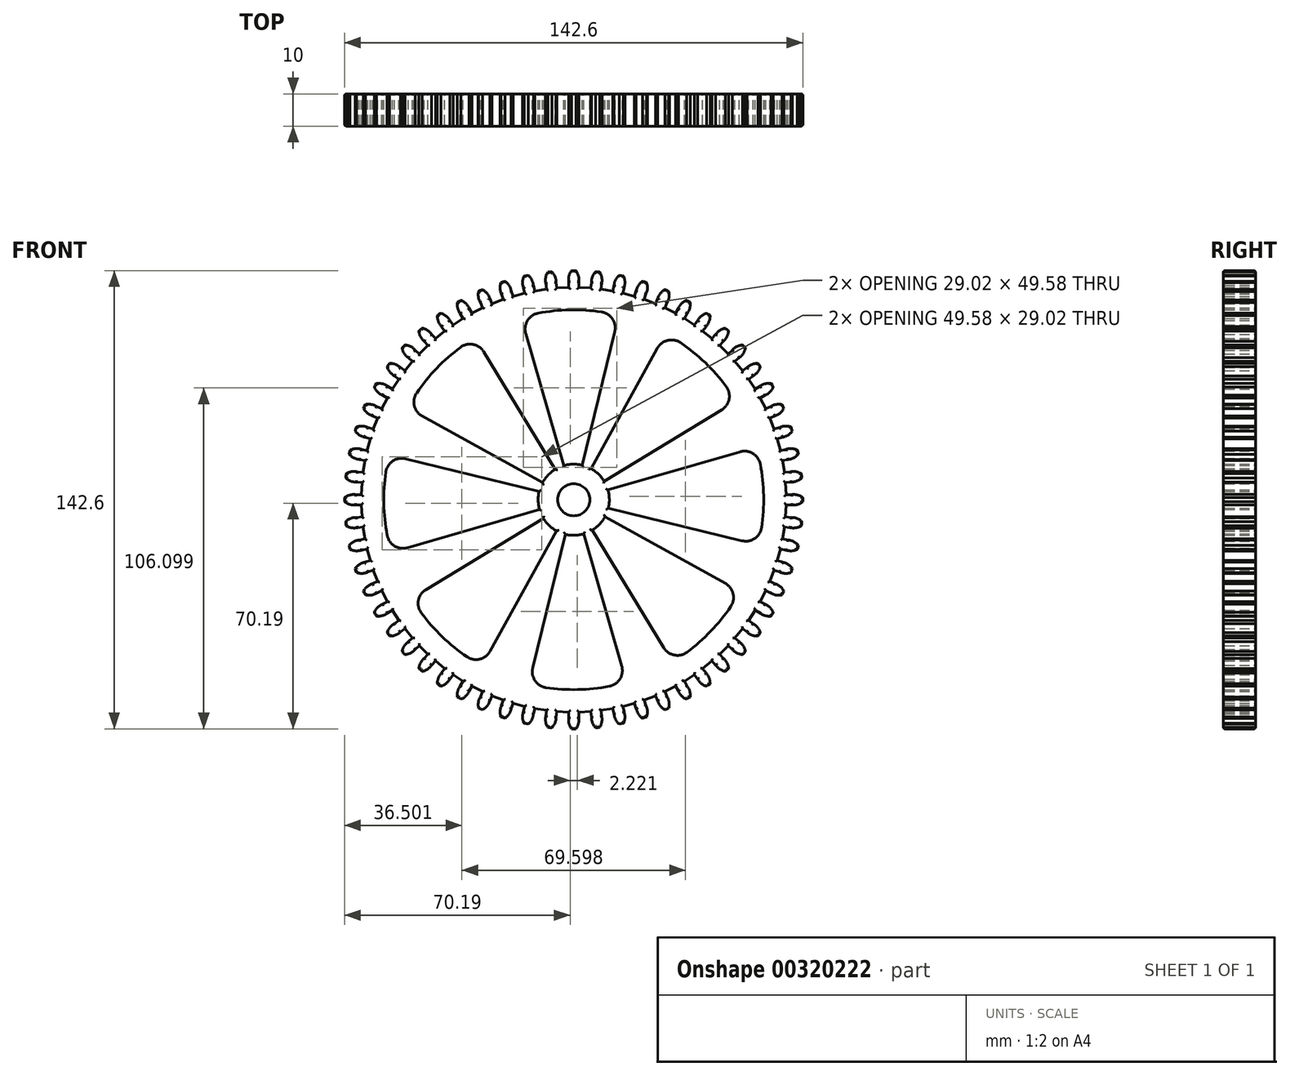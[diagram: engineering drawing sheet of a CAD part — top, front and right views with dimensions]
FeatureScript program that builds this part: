
annotation { "Feature Type Name" : "Feature", "Feature Type Description" : "" }
export const myFeature = defineFeature(function(context is Context, id is Id, definition is map)
    precondition{}
    {
        {
            var Q0;
            Q0=qCreatedBy(makeId("Front.planeOp"),FACE);
            var sketch = newSketch(context, id + "F0", { "sketchPlane" : qUnion([Q0])});
            skCircle(sketch, "E0", {"center": v(0, 0) * mm, "radius": 5 * mm});
            skLineSegment(sketch, "E1", {"start": v(1.6, 66.08) * mm, "end": v(1.6, 68.99) * mm});
            skArc(sketch, "E2", {"start": v(1.6, 67.83) * mm, "mid": v(1.47, 69.66) * mm, "end": v(0.66, 71.3) * mm});
            skLineSegment(sketch, "E3", {"start": v(0, 71.3) * mm, "end": v(0.66, 71.3) * mm});
            skLineSegment(sketch, "E4.MirrorCS", {"start": v(0, 71.3) * mm, "end": v(-0.66, 71.3) * mm});
            skArc(sketch, "E5.MirrorCS", {"start": v(-1.6, 67.83) * mm, "mid": v(-1.47, 69.66) * mm, "end": v(-0.66, 71.3) * mm});
            skLineSegment(sketch, "E6.MirrorCS", {"start": v(-1.6, 66.08) * mm, "end": v(-1.6, 68.99) * mm});
            skLineSegment(sketch, "E7.1.0", {"start": v(-8.5, 65.55) * mm, "end": v(-8.8, 68.44) * mm});
            skArc(sketch, "E7.1.1", {"start": v(-8.68, 67.3) * mm, "mid": v(-8.74, 69.12) * mm, "end": v(-8.1, 70.84) * mm});
            skLineSegment(sketch, "E7.1.2", {"start": v(-7.45, 70.9) * mm, "end": v(-8.1, 70.84) * mm});
            skLineSegment(sketch, "E7.1.3", {"start": v(-7.45, 70.9) * mm, "end": v(-6.8, 70.98) * mm});
            skArc(sketch, "E7.1.4", {"start": v(-5.5, 67.63) * mm, "mid": v(-5.82, 69.43) * mm, "end": v(-6.8, 70.98) * mm});
            skLineSegment(sketch, "E7.1.5", {"start": v(-5.32, 65.89) * mm, "end": v(-5.62, 68.78) * mm});
            skLineSegment(sketch, "E7.2.0", {"start": v(-15.3, 64.3) * mm, "end": v(-15.9, 67.15) * mm});
            skArc(sketch, "E7.2.1", {"start": v(-15.67, 66.02) * mm, "mid": v(-15.92, 67.83) * mm, "end": v(-15.47, 69.6) * mm});
            skLineSegment(sketch, "E7.2.2", {"start": v(-14.82, 69.74) * mm, "end": v(-15.47, 69.6) * mm});
            skLineSegment(sketch, "E7.2.3", {"start": v(-14.82, 69.74) * mm, "end": v(-14.18, 69.88) * mm});
            skArc(sketch, "E7.2.4", {"start": v(-12.54, 66.68) * mm, "mid": v(-13.05, 68.44) * mm, "end": v(-14.18, 69.88) * mm});
            skLineSegment(sketch, "E7.2.5", {"start": v(-12.17, 64.97) * mm, "end": v(-12.78, 67.81) * mm});
            skLineSegment(sketch, "E7.3.0", {"start": v(-21.94, 62.35) * mm, "end": v(-22.84, 65.12) * mm});
            skArc(sketch, "E7.3.1", {"start": v(-22.48, 64.02) * mm, "mid": v(-22.92, 65.8) * mm, "end": v(-22.66, 67.6) * mm});
            skLineSegment(sketch, "E7.3.2", {"start": v(-22.03, 67.81) * mm, "end": v(-22.66, 67.6) * mm});
            skLineSegment(sketch, "E7.3.3", {"start": v(-22.03, 67.81) * mm, "end": v(-21.4, 68.01) * mm});
            skArc(sketch, "E7.3.4", {"start": v(-19.44, 65) * mm, "mid": v(-20.13, 66.7) * mm, "end": v(-21.4, 68.01) * mm});
            skLineSegment(sketch, "E7.3.5", {"start": v(-18.9, 63.34) * mm, "end": v(-19.8, 66.1) * mm});
            skLineSegment(sketch, "E7.4.0", {"start": v(-28.34, 59.72) * mm, "end": v(-29.52, 62.37) * mm});
            skArc(sketch, "E7.4.1", {"start": v(-29.05, 61.32) * mm, "mid": v(-29.67, 63.04) * mm, "end": v(-29.6, 64.87) * mm});
            skLineSegment(sketch, "E7.4.2", {"start": v(-29, 65.14) * mm, "end": v(-29.6, 64.87) * mm});
            skLineSegment(sketch, "E7.4.3", {"start": v(-29, 65.14) * mm, "end": v(-28.4, 65.4) * mm});
            skArc(sketch, "E7.4.4", {"start": v(-26.13, 62.62) * mm, "mid": v(-26.99, 64.23) * mm, "end": v(-28.4, 65.4) * mm});
            skLineSegment(sketch, "E7.4.5", {"start": v(-25.42, 61.02) * mm, "end": v(-26.6, 63.68) * mm});
            skLineSegment(sketch, "E7.5.0", {"start": v(-34.43, 56.43) * mm, "end": v(-35.88, 58.95) * mm});
            skArc(sketch, "E7.5.1", {"start": v(-35.3, 57.94) * mm, "mid": v(-36.1, 59.59) * mm, "end": v(-36.22, 61.42) * mm});
            skLineSegment(sketch, "E7.5.2", {"start": v(-35.65, 61.75) * mm, "end": v(-36.22, 61.42) * mm});
            skLineSegment(sketch, "E7.5.3", {"start": v(-35.65, 61.75) * mm, "end": v(-35.08, 62.07) * mm});
            skArc(sketch, "E7.5.4", {"start": v(-32.53, 59.54) * mm, "mid": v(-33.56, 61.06) * mm, "end": v(-35.08, 62.07) * mm});
            skLineSegment(sketch, "E7.5.5", {"start": v(-31.65, 58.03) * mm, "end": v(-33.1, 60.55) * mm});
            skLineSegment(sketch, "E7.6.0", {"start": v(-40.14, 52.52) * mm, "end": v(-41.85, 54.87) * mm});
            skArc(sketch, "E7.6.1", {"start": v(-41.16, 53.94) * mm, "mid": v(-42.13, 55.49) * mm, "end": v(-42.44, 57.3) * mm});
            skLineSegment(sketch, "E7.6.2", {"start": v(-41.9, 57.68) * mm, "end": v(-42.44, 57.3) * mm});
            skLineSegment(sketch, "E7.6.3", {"start": v(-41.9, 57.68) * mm, "end": v(-41.38, 58.07) * mm});
            skArc(sketch, "E7.6.4", {"start": v(-38.58, 55.82) * mm, "mid": v(-39.75, 57.22) * mm, "end": v(-41.38, 58.07) * mm});
            skLineSegment(sketch, "E7.6.5", {"start": v(-37.55, 54.4) * mm, "end": v(-39.26, 56.75) * mm});
            skLineSegment(sketch, "E7.7.0", {"start": v(-45.4, 48.04) * mm, "end": v(-47.35, 50.2) * mm});
            skArc(sketch, "E7.7.1", {"start": v(-46.58, 49.34) * mm, "mid": v(-47.7, 50.78) * mm, "end": v(-48.2, 52.54) * mm});
            skLineSegment(sketch, "E7.7.2", {"start": v(-47.7, 52.99) * mm, "end": v(-48.2, 52.54) * mm});
            skLineSegment(sketch, "E7.7.3", {"start": v(-47.7, 52.99) * mm, "end": v(-47.22, 53.42) * mm});
            skArc(sketch, "E7.7.4", {"start": v(-44.2, 51.48) * mm, "mid": v(-45.52, 52.75) * mm, "end": v(-47.22, 53.42) * mm});
            skLineSegment(sketch, "E7.7.5", {"start": v(-43.03, 50.18) * mm, "end": v(-44.97, 52.34) * mm});
            skLineSegment(sketch, "E7.8.0", {"start": v(-50.18, 43.03) * mm, "end": v(-52.34, 44.97) * mm});
            skArc(sketch, "E7.8.1", {"start": v(-51.48, 44.2) * mm, "mid": v(-52.75, 45.52) * mm, "end": v(-53.42, 47.22) * mm});
            skLineSegment(sketch, "E7.8.2", {"start": v(-52.99, 47.7) * mm, "end": v(-53.42, 47.22) * mm});
            skLineSegment(sketch, "E7.8.3", {"start": v(-52.99, 47.7) * mm, "end": v(-52.54, 48.2) * mm});
            skArc(sketch, "E7.8.4", {"start": v(-49.34, 46.58) * mm, "mid": v(-50.78, 47.7) * mm, "end": v(-52.54, 48.2) * mm});
            skLineSegment(sketch, "E7.8.5", {"start": v(-48.04, 45.4) * mm, "end": v(-50.2, 47.35) * mm});
            skLineSegment(sketch, "E7.9.0", {"start": v(-54.4, 37.55) * mm, "end": v(-56.75, 39.26) * mm});
            skArc(sketch, "E7.9.1", {"start": v(-55.82, 38.58) * mm, "mid": v(-57.22, 39.75) * mm, "end": v(-58.07, 41.38) * mm});
            skLineSegment(sketch, "E7.9.2", {"start": v(-57.68, 41.9) * mm, "end": v(-58.07, 41.38) * mm});
            skLineSegment(sketch, "E7.9.3", {"start": v(-57.68, 41.9) * mm, "end": v(-57.3, 42.44) * mm});
            skArc(sketch, "E7.9.4", {"start": v(-53.94, 41.16) * mm, "mid": v(-55.49, 42.13) * mm, "end": v(-57.3, 42.44) * mm});
            skLineSegment(sketch, "E7.9.5", {"start": v(-52.52, 40.14) * mm, "end": v(-54.87, 41.85) * mm});
            skLineSegment(sketch, "E7.10.0", {"start": v(-58.03, 31.65) * mm, "end": v(-60.55, 33.1) * mm});
            skArc(sketch, "E7.10.1", {"start": v(-59.54, 32.53) * mm, "mid": v(-61.06, 33.56) * mm, "end": v(-62.07, 35.08) * mm});
            skLineSegment(sketch, "E7.10.2", {"start": v(-61.75, 35.65) * mm, "end": v(-62.07, 35.08) * mm});
            skLineSegment(sketch, "E7.10.3", {"start": v(-61.75, 35.65) * mm, "end": v(-61.42, 36.22) * mm});
            skArc(sketch, "E7.10.4", {"start": v(-57.94, 35.3) * mm, "mid": v(-59.59, 36.1) * mm, "end": v(-61.42, 36.22) * mm});
            skLineSegment(sketch, "E7.10.5", {"start": v(-56.43, 34.43) * mm, "end": v(-58.95, 35.88) * mm});
            skLineSegment(sketch, "E7.11.0", {"start": v(-61.02, 25.42) * mm, "end": v(-63.68, 26.6) * mm});
            skArc(sketch, "E7.11.1", {"start": v(-62.62, 26.13) * mm, "mid": v(-64.23, 26.99) * mm, "end": v(-65.4, 28.4) * mm});
            skLineSegment(sketch, "E7.11.2", {"start": v(-65.14, 29) * mm, "end": v(-65.4, 28.4) * mm});
            skLineSegment(sketch, "E7.11.3", {"start": v(-65.14, 29) * mm, "end": v(-64.87, 29.6) * mm});
            skArc(sketch, "E7.11.4", {"start": v(-61.32, 29.05) * mm, "mid": v(-63.04, 29.67) * mm, "end": v(-64.87, 29.6) * mm});
            skLineSegment(sketch, "E7.11.5", {"start": v(-59.72, 28.34) * mm, "end": v(-62.37, 29.52) * mm});
            skLineSegment(sketch, "E7.12.0", {"start": v(-63.34, 18.9) * mm, "end": v(-66.1, 19.8) * mm});
            skArc(sketch, "E7.12.1", {"start": v(-65, 19.44) * mm, "mid": v(-66.7, 20.13) * mm, "end": v(-68.01, 21.4) * mm});
            skLineSegment(sketch, "E7.12.2", {"start": v(-67.81, 22.03) * mm, "end": v(-68.01, 21.4) * mm});
            skLineSegment(sketch, "E7.12.3", {"start": v(-67.81, 22.03) * mm, "end": v(-67.6, 22.66) * mm});
            skArc(sketch, "E7.12.4", {"start": v(-64.02, 22.48) * mm, "mid": v(-65.8, 22.92) * mm, "end": v(-67.6, 22.66) * mm});
            skLineSegment(sketch, "E7.12.5", {"start": v(-62.35, 21.94) * mm, "end": v(-65.12, 22.84) * mm});
            skLineSegment(sketch, "E7.13.0", {"start": v(-64.97, 12.17) * mm, "end": v(-67.81, 12.78) * mm});
            skArc(sketch, "E7.13.1", {"start": v(-66.68, 12.54) * mm, "mid": v(-68.44, 13.05) * mm, "end": v(-69.88, 14.18) * mm});
            skLineSegment(sketch, "E7.13.2", {"start": v(-69.74, 14.82) * mm, "end": v(-69.88, 14.18) * mm});
            skLineSegment(sketch, "E7.13.3", {"start": v(-69.74, 14.82) * mm, "end": v(-69.6, 15.47) * mm});
            skArc(sketch, "E7.13.4", {"start": v(-66.02, 15.67) * mm, "mid": v(-67.83, 15.92) * mm, "end": v(-69.6, 15.47) * mm});
            skLineSegment(sketch, "E7.13.5", {"start": v(-64.3, 15.3) * mm, "end": v(-67.15, 15.9) * mm});
            skLineSegment(sketch, "E7.14.0", {"start": v(-65.89, 5.32) * mm, "end": v(-68.78, 5.62) * mm});
            skArc(sketch, "E7.14.1", {"start": v(-67.63, 5.5) * mm, "mid": v(-69.43, 5.82) * mm, "end": v(-70.98, 6.8) * mm});
            skLineSegment(sketch, "E7.14.2", {"start": v(-70.9, 7.45) * mm, "end": v(-70.98, 6.8) * mm});
            skLineSegment(sketch, "E7.14.3", {"start": v(-70.9, 7.45) * mm, "end": v(-70.84, 8.1) * mm});
            skArc(sketch, "E7.14.4", {"start": v(-67.3, 8.68) * mm, "mid": v(-69.12, 8.74) * mm, "end": v(-70.84, 8.1) * mm});
            skLineSegment(sketch, "E7.14.5", {"start": v(-65.55, 8.5) * mm, "end": v(-68.44, 8.8) * mm});
            skLineSegment(sketch, "E7.15.0", {"start": v(-66.08, -1.6) * mm, "end": v(-68.99, -1.6) * mm});
            skArc(sketch, "E7.15.1", {"start": v(-67.83, -1.6) * mm, "mid": v(-69.66, -1.47) * mm, "end": v(-71.3, -0.66) * mm});
            skLineSegment(sketch, "E7.15.2", {"start": v(-71.3, 0) * mm, "end": v(-71.3, -0.66) * mm});
            skLineSegment(sketch, "E7.15.3", {"start": v(-71.3, 0) * mm, "end": v(-71.3, 0.66) * mm});
            skArc(sketch, "E7.15.4", {"start": v(-67.83, 1.6) * mm, "mid": v(-69.66, 1.47) * mm, "end": v(-71.3, 0.66) * mm});
            skLineSegment(sketch, "E7.15.5", {"start": v(-66.08, 1.6) * mm, "end": v(-68.99, 1.6) * mm});
            skLineSegment(sketch, "E7.16.0", {"start": v(-65.55, -8.5) * mm, "end": v(-68.44, -8.8) * mm});
            skArc(sketch, "E7.16.1", {"start": v(-67.3, -8.68) * mm, "mid": v(-69.12, -8.74) * mm, "end": v(-70.84, -8.1) * mm});
            skLineSegment(sketch, "E7.16.2", {"start": v(-70.9, -7.45) * mm, "end": v(-70.84, -8.1) * mm});
            skLineSegment(sketch, "E7.16.3", {"start": v(-70.9, -7.45) * mm, "end": v(-70.98, -6.8) * mm});
            skArc(sketch, "E7.16.4", {"start": v(-67.63, -5.5) * mm, "mid": v(-69.43, -5.82) * mm, "end": v(-70.98, -6.8) * mm});
            skLineSegment(sketch, "E7.16.5", {"start": v(-65.89, -5.32) * mm, "end": v(-68.78, -5.62) * mm});
            skLineSegment(sketch, "E7.17.0", {"start": v(-64.3, -15.3) * mm, "end": v(-67.15, -15.9) * mm});
            skArc(sketch, "E7.17.1", {"start": v(-66.02, -15.67) * mm, "mid": v(-67.83, -15.92) * mm, "end": v(-69.6, -15.47) * mm});
            skLineSegment(sketch, "E7.17.2", {"start": v(-69.74, -14.82) * mm, "end": v(-69.6, -15.47) * mm});
            skLineSegment(sketch, "E7.17.3", {"start": v(-69.74, -14.82) * mm, "end": v(-69.88, -14.18) * mm});
            skArc(sketch, "E7.17.4", {"start": v(-66.68, -12.54) * mm, "mid": v(-68.44, -13.05) * mm, "end": v(-69.88, -14.18) * mm});
            skLineSegment(sketch, "E7.17.5", {"start": v(-64.97, -12.17) * mm, "end": v(-67.81, -12.78) * mm});
            skLineSegment(sketch, "E7.18.0", {"start": v(-62.35, -21.94) * mm, "end": v(-65.12, -22.84) * mm});
            skArc(sketch, "E7.18.1", {"start": v(-64.02, -22.48) * mm, "mid": v(-65.8, -22.92) * mm, "end": v(-67.6, -22.66) * mm});
            skLineSegment(sketch, "E7.18.2", {"start": v(-67.81, -22.03) * mm, "end": v(-67.6, -22.66) * mm});
            skLineSegment(sketch, "E7.18.3", {"start": v(-67.81, -22.03) * mm, "end": v(-68.01, -21.4) * mm});
            skArc(sketch, "E7.18.4", {"start": v(-65, -19.44) * mm, "mid": v(-66.7, -20.13) * mm, "end": v(-68.01, -21.4) * mm});
            skLineSegment(sketch, "E7.18.5", {"start": v(-63.34, -18.9) * mm, "end": v(-66.1, -19.8) * mm});
            skLineSegment(sketch, "E7.19.0", {"start": v(-59.72, -28.34) * mm, "end": v(-62.37, -29.52) * mm});
            skArc(sketch, "E7.19.1", {"start": v(-61.32, -29.05) * mm, "mid": v(-63.04, -29.67) * mm, "end": v(-64.87, -29.6) * mm});
            skLineSegment(sketch, "E7.19.2", {"start": v(-65.14, -29) * mm, "end": v(-64.87, -29.6) * mm});
            skLineSegment(sketch, "E7.19.3", {"start": v(-65.14, -29) * mm, "end": v(-65.4, -28.4) * mm});
            skArc(sketch, "E7.19.4", {"start": v(-62.62, -26.13) * mm, "mid": v(-64.23, -26.99) * mm, "end": v(-65.4, -28.4) * mm});
            skLineSegment(sketch, "E7.19.5", {"start": v(-61.02, -25.42) * mm, "end": v(-63.68, -26.6) * mm});
            skLineSegment(sketch, "E7.20.0", {"start": v(-56.43, -34.43) * mm, "end": v(-58.95, -35.88) * mm});
            skArc(sketch, "E7.20.1", {"start": v(-57.94, -35.3) * mm, "mid": v(-59.59, -36.1) * mm, "end": v(-61.42, -36.22) * mm});
            skLineSegment(sketch, "E7.20.2", {"start": v(-61.75, -35.65) * mm, "end": v(-61.42, -36.22) * mm});
            skLineSegment(sketch, "E7.20.3", {"start": v(-61.75, -35.65) * mm, "end": v(-62.07, -35.08) * mm});
            skArc(sketch, "E7.20.4", {"start": v(-59.54, -32.53) * mm, "mid": v(-61.06, -33.56) * mm, "end": v(-62.07, -35.08) * mm});
            skLineSegment(sketch, "E7.20.5", {"start": v(-58.03, -31.65) * mm, "end": v(-60.55, -33.1) * mm});
            skLineSegment(sketch, "E7.21.0", {"start": v(-52.52, -40.14) * mm, "end": v(-54.87, -41.85) * mm});
            skArc(sketch, "E7.21.1", {"start": v(-53.94, -41.16) * mm, "mid": v(-55.49, -42.13) * mm, "end": v(-57.3, -42.44) * mm});
            skLineSegment(sketch, "E7.21.2", {"start": v(-57.68, -41.9) * mm, "end": v(-57.3, -42.44) * mm});
            skLineSegment(sketch, "E7.21.3", {"start": v(-57.68, -41.9) * mm, "end": v(-58.07, -41.38) * mm});
            skArc(sketch, "E7.21.4", {"start": v(-55.82, -38.58) * mm, "mid": v(-57.22, -39.75) * mm, "end": v(-58.07, -41.38) * mm});
            skLineSegment(sketch, "E7.21.5", {"start": v(-54.4, -37.55) * mm, "end": v(-56.75, -39.26) * mm});
            skLineSegment(sketch, "E7.22.0", {"start": v(-48.04, -45.4) * mm, "end": v(-50.2, -47.35) * mm});
            skArc(sketch, "E7.22.1", {"start": v(-49.34, -46.58) * mm, "mid": v(-50.78, -47.7) * mm, "end": v(-52.54, -48.2) * mm});
            skLineSegment(sketch, "E7.22.2", {"start": v(-52.99, -47.7) * mm, "end": v(-52.54, -48.2) * mm});
            skLineSegment(sketch, "E7.22.3", {"start": v(-52.99, -47.7) * mm, "end": v(-53.42, -47.22) * mm});
            skArc(sketch, "E7.22.4", {"start": v(-51.48, -44.2) * mm, "mid": v(-52.75, -45.52) * mm, "end": v(-53.42, -47.22) * mm});
            skLineSegment(sketch, "E7.22.5", {"start": v(-50.18, -43.03) * mm, "end": v(-52.34, -44.97) * mm});
            skLineSegment(sketch, "E7.23.0", {"start": v(-43.03, -50.18) * mm, "end": v(-44.97, -52.34) * mm});
            skArc(sketch, "E7.23.1", {"start": v(-44.2, -51.48) * mm, "mid": v(-45.52, -52.75) * mm, "end": v(-47.22, -53.42) * mm});
            skLineSegment(sketch, "E7.23.2", {"start": v(-47.7, -52.99) * mm, "end": v(-47.22, -53.42) * mm});
            skLineSegment(sketch, "E7.23.3", {"start": v(-47.7, -52.99) * mm, "end": v(-48.2, -52.54) * mm});
            skArc(sketch, "E7.23.4", {"start": v(-46.58, -49.34) * mm, "mid": v(-47.7, -50.78) * mm, "end": v(-48.2, -52.54) * mm});
            skLineSegment(sketch, "E7.23.5", {"start": v(-45.4, -48.04) * mm, "end": v(-47.35, -50.2) * mm});
            skLineSegment(sketch, "E7.24.0", {"start": v(-37.55, -54.4) * mm, "end": v(-39.26, -56.75) * mm});
            skArc(sketch, "E7.24.1", {"start": v(-38.58, -55.82) * mm, "mid": v(-39.75, -57.22) * mm, "end": v(-41.38, -58.07) * mm});
            skLineSegment(sketch, "E7.24.2", {"start": v(-41.9, -57.68) * mm, "end": v(-41.38, -58.07) * mm});
            skLineSegment(sketch, "E7.24.3", {"start": v(-41.9, -57.68) * mm, "end": v(-42.44, -57.3) * mm});
            skArc(sketch, "E7.24.4", {"start": v(-41.16, -53.94) * mm, "mid": v(-42.13, -55.49) * mm, "end": v(-42.44, -57.3) * mm});
            skLineSegment(sketch, "E7.24.5", {"start": v(-40.14, -52.52) * mm, "end": v(-41.85, -54.87) * mm});
            skLineSegment(sketch, "E7.25.0", {"start": v(-31.65, -58.03) * mm, "end": v(-33.1, -60.55) * mm});
            skArc(sketch, "E7.25.1", {"start": v(-32.53, -59.54) * mm, "mid": v(-33.56, -61.06) * mm, "end": v(-35.08, -62.07) * mm});
            skLineSegment(sketch, "E7.25.2", {"start": v(-35.65, -61.75) * mm, "end": v(-35.08, -62.07) * mm});
            skLineSegment(sketch, "E7.25.3", {"start": v(-35.65, -61.75) * mm, "end": v(-36.22, -61.42) * mm});
            skArc(sketch, "E7.25.4", {"start": v(-35.3, -57.94) * mm, "mid": v(-36.1, -59.59) * mm, "end": v(-36.22, -61.42) * mm});
            skLineSegment(sketch, "E7.25.5", {"start": v(-34.43, -56.43) * mm, "end": v(-35.88, -58.95) * mm});
            skLineSegment(sketch, "E7.26.0", {"start": v(-25.42, -61.02) * mm, "end": v(-26.6, -63.68) * mm});
            skArc(sketch, "E7.26.1", {"start": v(-26.13, -62.62) * mm, "mid": v(-26.99, -64.23) * mm, "end": v(-28.4, -65.4) * mm});
            skLineSegment(sketch, "E7.26.2", {"start": v(-29, -65.14) * mm, "end": v(-28.4, -65.4) * mm});
            skLineSegment(sketch, "E7.26.3", {"start": v(-29, -65.14) * mm, "end": v(-29.6, -64.87) * mm});
            skArc(sketch, "E7.26.4", {"start": v(-29.05, -61.32) * mm, "mid": v(-29.67, -63.04) * mm, "end": v(-29.6, -64.87) * mm});
            skLineSegment(sketch, "E7.26.5", {"start": v(-28.34, -59.72) * mm, "end": v(-29.52, -62.37) * mm});
            skLineSegment(sketch, "E7.27.0", {"start": v(-18.9, -63.34) * mm, "end": v(-19.8, -66.1) * mm});
            skArc(sketch, "E7.27.1", {"start": v(-19.44, -65) * mm, "mid": v(-20.13, -66.7) * mm, "end": v(-21.4, -68.01) * mm});
            skLineSegment(sketch, "E7.27.2", {"start": v(-22.03, -67.81) * mm, "end": v(-21.4, -68.01) * mm});
            skLineSegment(sketch, "E7.27.3", {"start": v(-22.03, -67.81) * mm, "end": v(-22.66, -67.6) * mm});
            skArc(sketch, "E7.27.4", {"start": v(-22.48, -64.02) * mm, "mid": v(-22.92, -65.8) * mm, "end": v(-22.66, -67.6) * mm});
            skLineSegment(sketch, "E7.27.5", {"start": v(-21.94, -62.35) * mm, "end": v(-22.84, -65.12) * mm});
            skLineSegment(sketch, "E7.28.0", {"start": v(-12.17, -64.97) * mm, "end": v(-12.78, -67.81) * mm});
            skArc(sketch, "E7.28.1", {"start": v(-12.54, -66.68) * mm, "mid": v(-13.05, -68.44) * mm, "end": v(-14.18, -69.88) * mm});
            skLineSegment(sketch, "E7.28.2", {"start": v(-14.82, -69.74) * mm, "end": v(-14.18, -69.88) * mm});
            skLineSegment(sketch, "E7.28.3", {"start": v(-14.82, -69.74) * mm, "end": v(-15.47, -69.6) * mm});
            skArc(sketch, "E7.28.4", {"start": v(-15.67, -66.02) * mm, "mid": v(-15.92, -67.83) * mm, "end": v(-15.47, -69.6) * mm});
            skLineSegment(sketch, "E7.28.5", {"start": v(-15.3, -64.3) * mm, "end": v(-15.9, -67.15) * mm});
            skLineSegment(sketch, "E7.29.0", {"start": v(-5.32, -65.89) * mm, "end": v(-5.62, -68.78) * mm});
            skArc(sketch, "E7.29.1", {"start": v(-5.5, -67.63) * mm, "mid": v(-5.82, -69.43) * mm, "end": v(-6.8, -70.98) * mm});
            skLineSegment(sketch, "E7.29.2", {"start": v(-7.45, -70.9) * mm, "end": v(-6.8, -70.98) * mm});
            skLineSegment(sketch, "E7.29.3", {"start": v(-7.45, -70.9) * mm, "end": v(-8.1, -70.84) * mm});
            skArc(sketch, "E7.29.4", {"start": v(-8.68, -67.3) * mm, "mid": v(-8.74, -69.12) * mm, "end": v(-8.1, -70.84) * mm});
            skLineSegment(sketch, "E7.29.5", {"start": v(-8.5, -65.55) * mm, "end": v(-8.8, -68.44) * mm});
            skLineSegment(sketch, "E7.30.0", {"start": v(1.6, -66.08) * mm, "end": v(1.6, -68.99) * mm});
            skArc(sketch, "E7.30.1", {"start": v(1.6, -67.83) * mm, "mid": v(1.47, -69.66) * mm, "end": v(0.66, -71.3) * mm});
            skLineSegment(sketch, "E7.30.2", {"start": v(0, -71.3) * mm, "end": v(0.66, -71.3) * mm});
            skLineSegment(sketch, "E7.30.3", {"start": v(0, -71.3) * mm, "end": v(-0.66, -71.3) * mm});
            skArc(sketch, "E7.30.4", {"start": v(-1.6, -67.83) * mm, "mid": v(-1.47, -69.66) * mm, "end": v(-0.66, -71.3) * mm});
            skLineSegment(sketch, "E7.30.5", {"start": v(-1.6, -66.08) * mm, "end": v(-1.6, -68.99) * mm});
            skLineSegment(sketch, "E7.31.0", {"start": v(8.5, -65.55) * mm, "end": v(8.8, -68.44) * mm});
            skArc(sketch, "E7.31.1", {"start": v(8.68, -67.3) * mm, "mid": v(8.74, -69.12) * mm, "end": v(8.1, -70.84) * mm});
            skLineSegment(sketch, "E7.31.2", {"start": v(7.45, -70.9) * mm, "end": v(8.1, -70.84) * mm});
            skLineSegment(sketch, "E7.31.3", {"start": v(7.45, -70.9) * mm, "end": v(6.8, -70.98) * mm});
            skArc(sketch, "E7.31.4", {"start": v(5.5, -67.63) * mm, "mid": v(5.82, -69.43) * mm, "end": v(6.8, -70.98) * mm});
            skLineSegment(sketch, "E7.31.5", {"start": v(5.32, -65.89) * mm, "end": v(5.62, -68.78) * mm});
            skLineSegment(sketch, "E7.32.0", {"start": v(15.3, -64.3) * mm, "end": v(15.9, -67.15) * mm});
            skArc(sketch, "E7.32.1", {"start": v(15.67, -66.02) * mm, "mid": v(15.92, -67.83) * mm, "end": v(15.47, -69.6) * mm});
            skLineSegment(sketch, "E7.32.2", {"start": v(14.82, -69.74) * mm, "end": v(15.47, -69.6) * mm});
            skLineSegment(sketch, "E7.32.3", {"start": v(14.82, -69.74) * mm, "end": v(14.18, -69.88) * mm});
            skArc(sketch, "E7.32.4", {"start": v(12.54, -66.68) * mm, "mid": v(13.05, -68.44) * mm, "end": v(14.18, -69.88) * mm});
            skLineSegment(sketch, "E7.32.5", {"start": v(12.17, -64.97) * mm, "end": v(12.78, -67.81) * mm});
            skLineSegment(sketch, "E7.33.0", {"start": v(21.94, -62.35) * mm, "end": v(22.84, -65.12) * mm});
            skArc(sketch, "E7.33.1", {"start": v(22.48, -64.02) * mm, "mid": v(22.92, -65.8) * mm, "end": v(22.66, -67.6) * mm});
            skLineSegment(sketch, "E7.33.2", {"start": v(22.03, -67.81) * mm, "end": v(22.66, -67.6) * mm});
            skLineSegment(sketch, "E7.33.3", {"start": v(22.03, -67.81) * mm, "end": v(21.4, -68.01) * mm});
            skArc(sketch, "E7.33.4", {"start": v(19.44, -65) * mm, "mid": v(20.13, -66.7) * mm, "end": v(21.4, -68.01) * mm});
            skLineSegment(sketch, "E7.33.5", {"start": v(18.9, -63.34) * mm, "end": v(19.8, -66.1) * mm});
            skLineSegment(sketch, "E7.34.0", {"start": v(28.34, -59.72) * mm, "end": v(29.52, -62.37) * mm});
            skArc(sketch, "E7.34.1", {"start": v(29.05, -61.32) * mm, "mid": v(29.67, -63.04) * mm, "end": v(29.6, -64.87) * mm});
            skLineSegment(sketch, "E7.34.2", {"start": v(29, -65.14) * mm, "end": v(29.6, -64.87) * mm});
            skLineSegment(sketch, "E7.34.3", {"start": v(29, -65.14) * mm, "end": v(28.4, -65.4) * mm});
            skArc(sketch, "E7.34.4", {"start": v(26.13, -62.62) * mm, "mid": v(26.99, -64.23) * mm, "end": v(28.4, -65.4) * mm});
            skLineSegment(sketch, "E7.34.5", {"start": v(25.42, -61.02) * mm, "end": v(26.6, -63.68) * mm});
            skLineSegment(sketch, "E7.35.0", {"start": v(34.43, -56.43) * mm, "end": v(35.88, -58.95) * mm});
            skArc(sketch, "E7.35.1", {"start": v(35.3, -57.94) * mm, "mid": v(36.1, -59.59) * mm, "end": v(36.22, -61.42) * mm});
            skLineSegment(sketch, "E7.35.2", {"start": v(35.65, -61.75) * mm, "end": v(36.22, -61.42) * mm});
            skLineSegment(sketch, "E7.35.3", {"start": v(35.65, -61.75) * mm, "end": v(35.08, -62.07) * mm});
            skArc(sketch, "E7.35.4", {"start": v(32.53, -59.54) * mm, "mid": v(33.56, -61.06) * mm, "end": v(35.08, -62.07) * mm});
            skLineSegment(sketch, "E7.35.5", {"start": v(31.65, -58.03) * mm, "end": v(33.1, -60.55) * mm});
            skLineSegment(sketch, "E7.36.0", {"start": v(40.14, -52.52) * mm, "end": v(41.85, -54.87) * mm});
            skArc(sketch, "E7.36.1", {"start": v(41.16, -53.94) * mm, "mid": v(42.13, -55.49) * mm, "end": v(42.44, -57.3) * mm});
            skLineSegment(sketch, "E7.36.2", {"start": v(41.9, -57.68) * mm, "end": v(42.44, -57.3) * mm});
            skLineSegment(sketch, "E7.36.3", {"start": v(41.9, -57.68) * mm, "end": v(41.38, -58.07) * mm});
            skArc(sketch, "E7.36.4", {"start": v(38.58, -55.82) * mm, "mid": v(39.75, -57.22) * mm, "end": v(41.38, -58.07) * mm});
            skLineSegment(sketch, "E7.36.5", {"start": v(37.55, -54.4) * mm, "end": v(39.26, -56.75) * mm});
            skLineSegment(sketch, "E7.37.0", {"start": v(45.4, -48.04) * mm, "end": v(47.35, -50.2) * mm});
            skArc(sketch, "E7.37.1", {"start": v(46.58, -49.34) * mm, "mid": v(47.7, -50.78) * mm, "end": v(48.2, -52.54) * mm});
            skLineSegment(sketch, "E7.37.2", {"start": v(47.7, -52.99) * mm, "end": v(48.2, -52.54) * mm});
            skLineSegment(sketch, "E7.37.3", {"start": v(47.7, -52.99) * mm, "end": v(47.22, -53.42) * mm});
            skArc(sketch, "E7.37.4", {"start": v(44.2, -51.48) * mm, "mid": v(45.52, -52.75) * mm, "end": v(47.22, -53.42) * mm});
            skLineSegment(sketch, "E7.37.5", {"start": v(43.03, -50.18) * mm, "end": v(44.97, -52.34) * mm});
            skLineSegment(sketch, "E7.38.0", {"start": v(50.18, -43.03) * mm, "end": v(52.34, -44.97) * mm});
            skArc(sketch, "E7.38.1", {"start": v(51.48, -44.2) * mm, "mid": v(52.75, -45.52) * mm, "end": v(53.42, -47.22) * mm});
            skLineSegment(sketch, "E7.38.2", {"start": v(52.99, -47.7) * mm, "end": v(53.42, -47.22) * mm});
            skLineSegment(sketch, "E7.38.3", {"start": v(52.99, -47.7) * mm, "end": v(52.54, -48.2) * mm});
            skArc(sketch, "E7.38.4", {"start": v(49.34, -46.58) * mm, "mid": v(50.78, -47.7) * mm, "end": v(52.54, -48.2) * mm});
            skLineSegment(sketch, "E7.38.5", {"start": v(48.04, -45.4) * mm, "end": v(50.2, -47.35) * mm});
            skLineSegment(sketch, "E7.39.0", {"start": v(54.4, -37.55) * mm, "end": v(56.75, -39.26) * mm});
            skArc(sketch, "E7.39.1", {"start": v(55.82, -38.58) * mm, "mid": v(57.22, -39.75) * mm, "end": v(58.07, -41.38) * mm});
            skLineSegment(sketch, "E7.39.2", {"start": v(57.68, -41.9) * mm, "end": v(58.07, -41.38) * mm});
            skLineSegment(sketch, "E7.39.3", {"start": v(57.68, -41.9) * mm, "end": v(57.3, -42.44) * mm});
            skArc(sketch, "E7.39.4", {"start": v(53.94, -41.16) * mm, "mid": v(55.49, -42.13) * mm, "end": v(57.3, -42.44) * mm});
            skLineSegment(sketch, "E7.39.5", {"start": v(52.52, -40.14) * mm, "end": v(54.87, -41.85) * mm});
            skLineSegment(sketch, "E7.40.0", {"start": v(58.03, -31.65) * mm, "end": v(60.55, -33.1) * mm});
            skArc(sketch, "E7.40.1", {"start": v(59.54, -32.53) * mm, "mid": v(61.06, -33.56) * mm, "end": v(62.07, -35.08) * mm});
            skLineSegment(sketch, "E7.40.2", {"start": v(61.75, -35.65) * mm, "end": v(62.07, -35.08) * mm});
            skLineSegment(sketch, "E7.40.3", {"start": v(61.75, -35.65) * mm, "end": v(61.42, -36.22) * mm});
            skArc(sketch, "E7.40.4", {"start": v(57.94, -35.3) * mm, "mid": v(59.59, -36.1) * mm, "end": v(61.42, -36.22) * mm});
            skLineSegment(sketch, "E7.40.5", {"start": v(56.43, -34.43) * mm, "end": v(58.95, -35.88) * mm});
            skLineSegment(sketch, "E7.41.0", {"start": v(61.02, -25.42) * mm, "end": v(63.68, -26.6) * mm});
            skArc(sketch, "E7.41.1", {"start": v(62.62, -26.13) * mm, "mid": v(64.23, -26.99) * mm, "end": v(65.4, -28.4) * mm});
            skLineSegment(sketch, "E7.41.2", {"start": v(65.14, -29) * mm, "end": v(65.4, -28.4) * mm});
            skLineSegment(sketch, "E7.41.3", {"start": v(65.14, -29) * mm, "end": v(64.87, -29.6) * mm});
            skArc(sketch, "E7.41.4", {"start": v(61.32, -29.05) * mm, "mid": v(63.04, -29.67) * mm, "end": v(64.87, -29.6) * mm});
            skLineSegment(sketch, "E7.41.5", {"start": v(59.72, -28.34) * mm, "end": v(62.37, -29.52) * mm});
            skLineSegment(sketch, "E7.42.0", {"start": v(63.34, -18.9) * mm, "end": v(66.1, -19.8) * mm});
            skArc(sketch, "E7.42.1", {"start": v(65, -19.44) * mm, "mid": v(66.7, -20.13) * mm, "end": v(68.01, -21.4) * mm});
            skLineSegment(sketch, "E7.42.2", {"start": v(67.81, -22.03) * mm, "end": v(68.01, -21.4) * mm});
            skLineSegment(sketch, "E7.42.3", {"start": v(67.81, -22.03) * mm, "end": v(67.6, -22.66) * mm});
            skArc(sketch, "E7.42.4", {"start": v(64.02, -22.48) * mm, "mid": v(65.8, -22.92) * mm, "end": v(67.6, -22.66) * mm});
            skLineSegment(sketch, "E7.42.5", {"start": v(62.35, -21.94) * mm, "end": v(65.12, -22.84) * mm});
            skLineSegment(sketch, "E7.43.0", {"start": v(64.97, -12.17) * mm, "end": v(67.81, -12.78) * mm});
            skArc(sketch, "E7.43.1", {"start": v(66.68, -12.54) * mm, "mid": v(68.44, -13.05) * mm, "end": v(69.88, -14.18) * mm});
            skLineSegment(sketch, "E7.43.2", {"start": v(69.74, -14.82) * mm, "end": v(69.88, -14.18) * mm});
            skLineSegment(sketch, "E7.43.3", {"start": v(69.74, -14.82) * mm, "end": v(69.6, -15.47) * mm});
            skArc(sketch, "E7.43.4", {"start": v(66.02, -15.67) * mm, "mid": v(67.83, -15.92) * mm, "end": v(69.6, -15.47) * mm});
            skLineSegment(sketch, "E7.43.5", {"start": v(64.3, -15.3) * mm, "end": v(67.15, -15.9) * mm});
            skLineSegment(sketch, "E7.44.0", {"start": v(65.89, -5.32) * mm, "end": v(68.78, -5.62) * mm});
            skArc(sketch, "E7.44.1", {"start": v(67.63, -5.5) * mm, "mid": v(69.43, -5.82) * mm, "end": v(70.98, -6.8) * mm});
            skLineSegment(sketch, "E7.44.2", {"start": v(70.9, -7.45) * mm, "end": v(70.98, -6.8) * mm});
            skLineSegment(sketch, "E7.44.3", {"start": v(70.9, -7.45) * mm, "end": v(70.84, -8.1) * mm});
            skArc(sketch, "E7.44.4", {"start": v(67.3, -8.68) * mm, "mid": v(69.12, -8.74) * mm, "end": v(70.84, -8.1) * mm});
            skLineSegment(sketch, "E7.44.5", {"start": v(65.55, -8.5) * mm, "end": v(68.44, -8.8) * mm});
            skLineSegment(sketch, "E7.45.0", {"start": v(66.08, 1.6) * mm, "end": v(68.99, 1.6) * mm});
            skArc(sketch, "E7.45.1", {"start": v(67.83, 1.6) * mm, "mid": v(69.66, 1.47) * mm, "end": v(71.3, 0.66) * mm});
            skLineSegment(sketch, "E7.45.2", {"start": v(71.3, 0) * mm, "end": v(71.3, 0.66) * mm});
            skLineSegment(sketch, "E7.45.3", {"start": v(71.3, 0) * mm, "end": v(71.3, -0.66) * mm});
            skArc(sketch, "E7.45.4", {"start": v(67.83, -1.6) * mm, "mid": v(69.66, -1.47) * mm, "end": v(71.3, -0.66) * mm});
            skLineSegment(sketch, "E7.45.5", {"start": v(66.08, -1.6) * mm, "end": v(68.99, -1.6) * mm});
            skLineSegment(sketch, "E7.46.0", {"start": v(65.55, 8.5) * mm, "end": v(68.44, 8.8) * mm});
            skArc(sketch, "E7.46.1", {"start": v(67.3, 8.68) * mm, "mid": v(69.12, 8.74) * mm, "end": v(70.84, 8.1) * mm});
            skLineSegment(sketch, "E7.46.2", {"start": v(70.9, 7.45) * mm, "end": v(70.84, 8.1) * mm});
            skLineSegment(sketch, "E7.46.3", {"start": v(70.9, 7.45) * mm, "end": v(70.98, 6.8) * mm});
            skArc(sketch, "E7.46.4", {"start": v(67.63, 5.5) * mm, "mid": v(69.43, 5.82) * mm, "end": v(70.98, 6.8) * mm});
            skLineSegment(sketch, "E7.46.5", {"start": v(65.89, 5.32) * mm, "end": v(68.78, 5.62) * mm});
            skLineSegment(sketch, "E7.47.0", {"start": v(64.3, 15.3) * mm, "end": v(67.15, 15.9) * mm});
            skArc(sketch, "E7.47.1", {"start": v(66.02, 15.67) * mm, "mid": v(67.83, 15.92) * mm, "end": v(69.6, 15.47) * mm});
            skLineSegment(sketch, "E7.47.2", {"start": v(69.74, 14.82) * mm, "end": v(69.6, 15.47) * mm});
            skLineSegment(sketch, "E7.47.3", {"start": v(69.74, 14.82) * mm, "end": v(69.88, 14.18) * mm});
            skArc(sketch, "E7.47.4", {"start": v(66.68, 12.54) * mm, "mid": v(68.44, 13.05) * mm, "end": v(69.88, 14.18) * mm});
            skLineSegment(sketch, "E7.47.5", {"start": v(64.97, 12.17) * mm, "end": v(67.81, 12.78) * mm});
            skLineSegment(sketch, "E7.48.0", {"start": v(62.35, 21.94) * mm, "end": v(65.12, 22.84) * mm});
            skArc(sketch, "E7.48.1", {"start": v(64.02, 22.48) * mm, "mid": v(65.8, 22.92) * mm, "end": v(67.6, 22.66) * mm});
            skLineSegment(sketch, "E7.48.2", {"start": v(67.81, 22.03) * mm, "end": v(67.6, 22.66) * mm});
            skLineSegment(sketch, "E7.48.3", {"start": v(67.81, 22.03) * mm, "end": v(68.01, 21.4) * mm});
            skArc(sketch, "E7.48.4", {"start": v(65, 19.44) * mm, "mid": v(66.7, 20.13) * mm, "end": v(68.01, 21.4) * mm});
            skLineSegment(sketch, "E7.48.5", {"start": v(63.34, 18.9) * mm, "end": v(66.1, 19.8) * mm});
            skLineSegment(sketch, "E7.49.0", {"start": v(59.72, 28.34) * mm, "end": v(62.37, 29.52) * mm});
            skArc(sketch, "E7.49.1", {"start": v(61.32, 29.05) * mm, "mid": v(63.04, 29.67) * mm, "end": v(64.87, 29.6) * mm});
            skLineSegment(sketch, "E7.49.2", {"start": v(65.14, 29) * mm, "end": v(64.87, 29.6) * mm});
            skLineSegment(sketch, "E7.49.3", {"start": v(65.14, 29) * mm, "end": v(65.4, 28.4) * mm});
            skArc(sketch, "E7.49.4", {"start": v(62.62, 26.13) * mm, "mid": v(64.23, 26.99) * mm, "end": v(65.4, 28.4) * mm});
            skLineSegment(sketch, "E7.49.5", {"start": v(61.02, 25.42) * mm, "end": v(63.68, 26.6) * mm});
            skLineSegment(sketch, "E7.50.0", {"start": v(56.43, 34.43) * mm, "end": v(58.95, 35.88) * mm});
            skArc(sketch, "E7.50.1", {"start": v(57.94, 35.3) * mm, "mid": v(59.59, 36.1) * mm, "end": v(61.42, 36.22) * mm});
            skLineSegment(sketch, "E7.50.2", {"start": v(61.75, 35.65) * mm, "end": v(61.42, 36.22) * mm});
            skLineSegment(sketch, "E7.50.3", {"start": v(61.75, 35.65) * mm, "end": v(62.07, 35.08) * mm});
            skArc(sketch, "E7.50.4", {"start": v(59.54, 32.53) * mm, "mid": v(61.06, 33.56) * mm, "end": v(62.07, 35.08) * mm});
            skLineSegment(sketch, "E7.50.5", {"start": v(58.03, 31.65) * mm, "end": v(60.55, 33.1) * mm});
            skLineSegment(sketch, "E7.51.0", {"start": v(52.52, 40.14) * mm, "end": v(54.87, 41.85) * mm});
            skArc(sketch, "E7.51.1", {"start": v(53.94, 41.16) * mm, "mid": v(55.49, 42.13) * mm, "end": v(57.3, 42.44) * mm});
            skLineSegment(sketch, "E7.51.2", {"start": v(57.68, 41.9) * mm, "end": v(57.3, 42.44) * mm});
            skLineSegment(sketch, "E7.51.3", {"start": v(57.68, 41.9) * mm, "end": v(58.07, 41.38) * mm});
            skArc(sketch, "E7.51.4", {"start": v(55.82, 38.58) * mm, "mid": v(57.22, 39.75) * mm, "end": v(58.07, 41.38) * mm});
            skLineSegment(sketch, "E7.51.5", {"start": v(54.4, 37.55) * mm, "end": v(56.75, 39.26) * mm});
            skLineSegment(sketch, "E7.52.0", {"start": v(48.04, 45.4) * mm, "end": v(50.2, 47.35) * mm});
            skArc(sketch, "E7.52.1", {"start": v(49.34, 46.58) * mm, "mid": v(50.78, 47.7) * mm, "end": v(52.54, 48.2) * mm});
            skLineSegment(sketch, "E7.52.2", {"start": v(52.99, 47.7) * mm, "end": v(52.54, 48.2) * mm});
            skLineSegment(sketch, "E7.52.3", {"start": v(52.99, 47.7) * mm, "end": v(53.42, 47.22) * mm});
            skArc(sketch, "E7.52.4", {"start": v(51.48, 44.2) * mm, "mid": v(52.75, 45.52) * mm, "end": v(53.42, 47.22) * mm});
            skLineSegment(sketch, "E7.52.5", {"start": v(50.18, 43.03) * mm, "end": v(52.34, 44.97) * mm});
            skLineSegment(sketch, "E7.53.0", {"start": v(43.03, 50.18) * mm, "end": v(44.97, 52.34) * mm});
            skArc(sketch, "E7.53.1", {"start": v(44.2, 51.48) * mm, "mid": v(45.52, 52.75) * mm, "end": v(47.22, 53.42) * mm});
            skLineSegment(sketch, "E7.53.2", {"start": v(47.7, 52.99) * mm, "end": v(47.22, 53.42) * mm});
            skLineSegment(sketch, "E7.53.3", {"start": v(47.7, 52.99) * mm, "end": v(48.2, 52.54) * mm});
            skArc(sketch, "E7.53.4", {"start": v(46.58, 49.34) * mm, "mid": v(47.7, 50.78) * mm, "end": v(48.2, 52.54) * mm});
            skLineSegment(sketch, "E7.53.5", {"start": v(45.4, 48.04) * mm, "end": v(47.35, 50.2) * mm});
            skLineSegment(sketch, "E7.54.0", {"start": v(37.55, 54.4) * mm, "end": v(39.26, 56.75) * mm});
            skArc(sketch, "E7.54.1", {"start": v(38.58, 55.82) * mm, "mid": v(39.75, 57.22) * mm, "end": v(41.38, 58.07) * mm});
            skLineSegment(sketch, "E7.54.2", {"start": v(41.9, 57.68) * mm, "end": v(41.38, 58.07) * mm});
            skLineSegment(sketch, "E7.54.3", {"start": v(41.9, 57.68) * mm, "end": v(42.44, 57.3) * mm});
            skArc(sketch, "E7.54.4", {"start": v(41.16, 53.94) * mm, "mid": v(42.13, 55.49) * mm, "end": v(42.44, 57.3) * mm});
            skLineSegment(sketch, "E7.54.5", {"start": v(40.14, 52.52) * mm, "end": v(41.85, 54.87) * mm});
            skLineSegment(sketch, "E7.55.0", {"start": v(31.65, 58.03) * mm, "end": v(33.1, 60.55) * mm});
            skArc(sketch, "E7.55.1", {"start": v(32.53, 59.54) * mm, "mid": v(33.56, 61.06) * mm, "end": v(35.08, 62.07) * mm});
            skLineSegment(sketch, "E7.55.2", {"start": v(35.65, 61.75) * mm, "end": v(35.08, 62.07) * mm});
            skLineSegment(sketch, "E7.55.3", {"start": v(35.65, 61.75) * mm, "end": v(36.22, 61.42) * mm});
            skArc(sketch, "E7.55.4", {"start": v(35.3, 57.94) * mm, "mid": v(36.1, 59.59) * mm, "end": v(36.22, 61.42) * mm});
            skLineSegment(sketch, "E7.55.5", {"start": v(34.43, 56.43) * mm, "end": v(35.88, 58.95) * mm});
            skLineSegment(sketch, "E7.56.0", {"start": v(25.42, 61.02) * mm, "end": v(26.6, 63.68) * mm});
            skArc(sketch, "E7.56.1", {"start": v(26.13, 62.62) * mm, "mid": v(26.99, 64.23) * mm, "end": v(28.4, 65.4) * mm});
            skLineSegment(sketch, "E7.56.2", {"start": v(29, 65.14) * mm, "end": v(28.4, 65.4) * mm});
            skLineSegment(sketch, "E7.56.3", {"start": v(29, 65.14) * mm, "end": v(29.6, 64.87) * mm});
            skArc(sketch, "E7.56.4", {"start": v(29.05, 61.32) * mm, "mid": v(29.67, 63.04) * mm, "end": v(29.6, 64.87) * mm});
            skLineSegment(sketch, "E7.56.5", {"start": v(28.34, 59.72) * mm, "end": v(29.52, 62.37) * mm});
            skLineSegment(sketch, "E7.57.0", {"start": v(18.9, 63.34) * mm, "end": v(19.8, 66.1) * mm});
            skArc(sketch, "E7.57.1", {"start": v(19.44, 65) * mm, "mid": v(20.13, 66.7) * mm, "end": v(21.4, 68.01) * mm});
            skLineSegment(sketch, "E7.57.2", {"start": v(22.03, 67.81) * mm, "end": v(21.4, 68.01) * mm});
            skLineSegment(sketch, "E7.57.3", {"start": v(22.03, 67.81) * mm, "end": v(22.66, 67.6) * mm});
            skArc(sketch, "E7.57.4", {"start": v(22.48, 64.02) * mm, "mid": v(22.92, 65.8) * mm, "end": v(22.66, 67.6) * mm});
            skLineSegment(sketch, "E7.57.5", {"start": v(21.94, 62.35) * mm, "end": v(22.84, 65.12) * mm});
            skLineSegment(sketch, "E7.58.0", {"start": v(12.17, 64.97) * mm, "end": v(12.78, 67.81) * mm});
            skArc(sketch, "E7.58.1", {"start": v(12.54, 66.68) * mm, "mid": v(13.05, 68.44) * mm, "end": v(14.18, 69.88) * mm});
            skLineSegment(sketch, "E7.58.2", {"start": v(14.82, 69.74) * mm, "end": v(14.18, 69.88) * mm});
            skLineSegment(sketch, "E7.58.3", {"start": v(14.82, 69.74) * mm, "end": v(15.47, 69.6) * mm});
            skArc(sketch, "E7.58.4", {"start": v(15.67, 66.02) * mm, "mid": v(15.92, 67.83) * mm, "end": v(15.47, 69.6) * mm});
            skLineSegment(sketch, "E7.58.5", {"start": v(15.3, 64.3) * mm, "end": v(15.9, 67.15) * mm});
            skLineSegment(sketch, "E7.59.0", {"start": v(5.32, 65.89) * mm, "end": v(5.62, 68.78) * mm});
            skArc(sketch, "E7.59.1", {"start": v(5.5, 67.63) * mm, "mid": v(5.82, 69.43) * mm, "end": v(6.8, 70.98) * mm});
            skLineSegment(sketch, "E7.59.2", {"start": v(7.45, 70.9) * mm, "end": v(6.8, 70.98) * mm});
            skLineSegment(sketch, "E7.59.3", {"start": v(7.45, 70.9) * mm, "end": v(8.1, 70.84) * mm});
            skArc(sketch, "E7.59.4", {"start": v(8.68, 67.3) * mm, "mid": v(8.74, 69.12) * mm, "end": v(8.1, 70.84) * mm});
            skLineSegment(sketch, "E7.59.5", {"start": v(8.5, 65.55) * mm, "end": v(8.8, 68.44) * mm});
            skArc(sketch, "E8", {"start": v(-48.88, 33.22) * mm, "mid": v(-42.66, 40.9) * mm, "end": v(-35.24, 47.45) * mm});
            skPoint(sketch, "E9.visualSharp", {"position": v(-58.68, 7) * mm});
            skPoint(sketch, "E10.MirrorP", {"position": v(-7, -58.68) * mm});
            skLineSegment(sketch, "E11", {"start": v(-5.32, 65.89) * mm, "end": v(-1.6, 66.08) * mm});
            skLineSegment(sketch, "E12.1.0", {"start": v(-12.17, 64.97) * mm, "end": v(-8.5, 65.55) * mm});
            skLineSegment(sketch, "E12.2.0", {"start": v(-18.9, 63.34) * mm, "end": v(-15.3, 64.3) * mm});
            skLineSegment(sketch, "E12.3.0", {"start": v(-25.42, 61.02) * mm, "end": v(-21.94, 62.35) * mm});
            skLineSegment(sketch, "E12.4.0", {"start": v(-31.65, 58.03) * mm, "end": v(-28.34, 59.72) * mm});
            skLineSegment(sketch, "E12.5.0", {"start": v(-37.55, 54.4) * mm, "end": v(-34.43, 56.43) * mm});
            skLineSegment(sketch, "E12.6.0", {"start": v(-43.03, 50.18) * mm, "end": v(-40.14, 52.52) * mm});
            skLineSegment(sketch, "E12.7.0", {"start": v(-48.04, 45.4) * mm, "end": v(-45.4, 48.04) * mm});
            skLineSegment(sketch, "E12.8.0", {"start": v(-52.52, 40.14) * mm, "end": v(-50.18, 43.03) * mm});
            skLineSegment(sketch, "E12.9.0", {"start": v(-56.43, 34.43) * mm, "end": v(-54.4, 37.55) * mm});
            skLineSegment(sketch, "E12.10.0", {"start": v(-59.72, 28.34) * mm, "end": v(-58.03, 31.65) * mm});
            skLineSegment(sketch, "E12.11.0", {"start": v(-62.35, 21.94) * mm, "end": v(-61.02, 25.42) * mm});
            skLineSegment(sketch, "E12.12.0", {"start": v(-64.3, 15.3) * mm, "end": v(-63.34, 18.9) * mm});
            skLineSegment(sketch, "E12.13.0", {"start": v(-65.55, 8.5) * mm, "end": v(-64.97, 12.17) * mm});
            skLineSegment(sketch, "E12.14.0", {"start": v(-66.08, 1.6) * mm, "end": v(-65.89, 5.32) * mm});
            skLineSegment(sketch, "E12.15.0", {"start": v(-65.89, -5.32) * mm, "end": v(-66.08, -1.6) * mm});
            skLineSegment(sketch, "E12.16.0", {"start": v(-64.97, -12.17) * mm, "end": v(-65.55, -8.5) * mm});
            skLineSegment(sketch, "E12.17.0", {"start": v(-63.34, -18.9) * mm, "end": v(-64.3, -15.3) * mm});
            skLineSegment(sketch, "E12.18.0", {"start": v(-61.02, -25.42) * mm, "end": v(-62.35, -21.94) * mm});
            skLineSegment(sketch, "E12.19.0", {"start": v(-58.03, -31.65) * mm, "end": v(-59.72, -28.34) * mm});
            skLineSegment(sketch, "E12.20.0", {"start": v(-54.4, -37.55) * mm, "end": v(-56.43, -34.43) * mm});
            skLineSegment(sketch, "E12.21.0", {"start": v(-50.18, -43.03) * mm, "end": v(-52.52, -40.14) * mm});
            skLineSegment(sketch, "E12.22.0", {"start": v(-45.4, -48.04) * mm, "end": v(-48.04, -45.4) * mm});
            skLineSegment(sketch, "E12.23.0", {"start": v(-40.14, -52.52) * mm, "end": v(-43.03, -50.18) * mm});
            skLineSegment(sketch, "E12.24.0", {"start": v(-34.43, -56.43) * mm, "end": v(-37.55, -54.4) * mm});
            skLineSegment(sketch, "E12.25.0", {"start": v(-28.34, -59.72) * mm, "end": v(-31.65, -58.03) * mm});
            skLineSegment(sketch, "E12.26.0", {"start": v(-21.94, -62.35) * mm, "end": v(-25.42, -61.02) * mm});
            skLineSegment(sketch, "E12.27.0", {"start": v(-15.3, -64.3) * mm, "end": v(-18.9, -63.34) * mm});
            skLineSegment(sketch, "E12.28.0", {"start": v(-8.5, -65.55) * mm, "end": v(-12.17, -64.97) * mm});
            skLineSegment(sketch, "E12.29.0", {"start": v(-1.6, -66.08) * mm, "end": v(-5.32, -65.89) * mm});
            skLineSegment(sketch, "E12.30.0", {"start": v(5.32, -65.89) * mm, "end": v(1.6, -66.08) * mm});
            skLineSegment(sketch, "E12.31.0", {"start": v(12.17, -64.97) * mm, "end": v(8.5, -65.55) * mm});
            skLineSegment(sketch, "E12.32.0", {"start": v(18.9, -63.34) * mm, "end": v(15.3, -64.3) * mm});
            skLineSegment(sketch, "E12.33.0", {"start": v(25.42, -61.02) * mm, "end": v(21.94, -62.35) * mm});
            skLineSegment(sketch, "E12.34.0", {"start": v(31.65, -58.03) * mm, "end": v(28.34, -59.72) * mm});
            skLineSegment(sketch, "E12.35.0", {"start": v(37.55, -54.4) * mm, "end": v(34.43, -56.43) * mm});
            skLineSegment(sketch, "E12.36.0", {"start": v(43.03, -50.18) * mm, "end": v(40.14, -52.52) * mm});
            skLineSegment(sketch, "E12.37.0", {"start": v(48.04, -45.4) * mm, "end": v(45.4, -48.04) * mm});
            skLineSegment(sketch, "E12.38.0", {"start": v(52.52, -40.14) * mm, "end": v(50.18, -43.03) * mm});
            skLineSegment(sketch, "E12.39.0", {"start": v(56.43, -34.43) * mm, "end": v(54.4, -37.55) * mm});
            skLineSegment(sketch, "E12.40.0", {"start": v(59.72, -28.34) * mm, "end": v(58.03, -31.65) * mm});
            skLineSegment(sketch, "E12.41.0", {"start": v(62.35, -21.94) * mm, "end": v(61.02, -25.42) * mm});
            skLineSegment(sketch, "E12.42.0", {"start": v(64.3, -15.3) * mm, "end": v(63.34, -18.9) * mm});
            skLineSegment(sketch, "E12.43.0", {"start": v(65.55, -8.5) * mm, "end": v(64.97, -12.17) * mm});
            skLineSegment(sketch, "E12.44.0", {"start": v(66.08, -1.6) * mm, "end": v(65.89, -5.32) * mm});
            skLineSegment(sketch, "E12.45.0", {"start": v(65.89, 5.32) * mm, "end": v(66.08, 1.6) * mm});
            skLineSegment(sketch, "E12.46.0", {"start": v(64.97, 12.17) * mm, "end": v(65.55, 8.5) * mm});
            skLineSegment(sketch, "E12.47.0", {"start": v(63.34, 18.9) * mm, "end": v(64.3, 15.3) * mm});
            skLineSegment(sketch, "E12.48.0", {"start": v(61.02, 25.42) * mm, "end": v(62.35, 21.94) * mm});
            skLineSegment(sketch, "E12.49.0", {"start": v(58.03, 31.65) * mm, "end": v(59.72, 28.34) * mm});
            skLineSegment(sketch, "E12.50.0", {"start": v(54.4, 37.55) * mm, "end": v(56.43, 34.43) * mm});
            skLineSegment(sketch, "E12.51.0", {"start": v(50.18, 43.03) * mm, "end": v(52.52, 40.14) * mm});
            skLineSegment(sketch, "E12.52.0", {"start": v(45.4, 48.04) * mm, "end": v(48.04, 45.4) * mm});
            skLineSegment(sketch, "E12.53.0", {"start": v(40.14, 52.52) * mm, "end": v(43.03, 50.18) * mm});
            skLineSegment(sketch, "E12.54.0", {"start": v(34.43, 56.43) * mm, "end": v(37.55, 54.4) * mm});
            skLineSegment(sketch, "E12.55.0", {"start": v(28.34, 59.72) * mm, "end": v(31.65, 58.03) * mm});
            skLineSegment(sketch, "E12.56.0", {"start": v(21.94, 62.35) * mm, "end": v(25.42, 61.02) * mm});
            skLineSegment(sketch, "E12.57.0", {"start": v(15.3, 64.3) * mm, "end": v(18.9, 63.34) * mm});
            skLineSegment(sketch, "E12.58.0", {"start": v(8.5, 65.55) * mm, "end": v(12.17, 64.97) * mm});
            skLineSegment(sketch, "E12.59.0", {"start": v(1.6, 66.08) * mm, "end": v(5.32, 65.89) * mm});
            skLineSegment(sketch, "E13", {"start": v(0, 0) * mm, "end": v(-4.38, 2.42) * mm});
            skArc(sketch, "E14", {"start": v(-5.75, 9.46) * mm, "mid": v(-8, 7.67) * mm, "end": v(-9.7, 5.35) * mm});
            skLineSegment(sketch, "E15.trimOffspring", {"start": v(-9.7, 5.35) * mm, "end": v(-47.16, 26.03) * mm});
            skLineSegment(sketch, "E16.trimOffspring", {"start": v(-5.75, 9.46) * mm, "end": v(-27.98, 46.03) * mm});
            skPoint(sketch, "E17.visualSharp", {"position": v(-30.7, 50.5) * mm});
            skArc(sketch, "E17.filletArc", {"start": v(-27.98, 46.03) * mm, "mid": v(-31.3, 48.34) * mm, "end": v(-35.24, 47.45) * mm});
            skPoint(sketch, "E18.visualSharp", {"position": v(-51.74, 28.56) * mm});
            skArc(sketch, "E18.filletArc", {"start": v(-48.88, 33.22) * mm, "mid": v(-49.6, 29.25) * mm, "end": v(-47.16, 26.03) * mm});
            skArc(sketch, "E19.1.0", {"start": v(-58.05, -11.07) * mm, "mid": v(-55.76, -14.4) * mm, "end": v(-51.76, -14.94) * mm});
            skArc(sketch, "E19.1.1", {"start": v(-58.05, -11.07) * mm, "mid": v(-59.09, -1.24) * mm, "end": v(-58.47, 8.63) * mm});
            skArc(sketch, "E19.1.2", {"start": v(-52.34, 12.76) * mm, "mid": v(-56.31, 12.05) * mm, "end": v(-58.47, 8.63) * mm});
            skLineSegment(sketch, "E19.1.3", {"start": v(-10.76, 2.62) * mm, "end": v(-52.34, 12.76) * mm});
            skArc(sketch, "E19.1.4", {"start": v(-10.76, 2.62) * mm, "mid": v(-11.07, -0.23) * mm, "end": v(-10.64, -3.07) * mm});
            skLineSegment(sketch, "E19.1.5", {"start": v(-10.64, -3.07) * mm, "end": v(-51.76, -14.94) * mm});
            skArc(sketch, "E19.2.0", {"start": v(-33.22, -48.88) * mm, "mid": v(-29.25, -49.6) * mm, "end": v(-26.03, -47.16) * mm});
            skArc(sketch, "E19.2.1", {"start": v(-33.22, -48.88) * mm, "mid": v(-40.9, -42.66) * mm, "end": v(-47.45, -35.24) * mm});
            skArc(sketch, "E19.2.2", {"start": v(-46.03, -27.98) * mm, "mid": v(-48.34, -31.3) * mm, "end": v(-47.45, -35.24) * mm});
            skLineSegment(sketch, "E19.2.3", {"start": v(-9.46, -5.75) * mm, "end": v(-46.03, -27.98) * mm});
            skArc(sketch, "E19.2.4", {"start": v(-9.46, -5.75) * mm, "mid": v(-7.67, -8) * mm, "end": v(-5.35, -9.7) * mm});
            skLineSegment(sketch, "E19.2.5", {"start": v(-5.35, -9.7) * mm, "end": v(-26.03, -47.16) * mm});
            skArc(sketch, "E19.3.0", {"start": v(11.07, -58.05) * mm, "mid": v(14.4, -55.76) * mm, "end": v(14.94, -51.76) * mm});
            skArc(sketch, "E19.3.1", {"start": v(11.07, -58.05) * mm, "mid": v(1.24, -59.09) * mm, "end": v(-8.63, -58.47) * mm});
            skArc(sketch, "E19.3.2", {"start": v(-12.76, -52.34) * mm, "mid": v(-12.05, -56.31) * mm, "end": v(-8.63, -58.47) * mm});
            skLineSegment(sketch, "E19.3.3", {"start": v(-2.62, -10.76) * mm, "end": v(-12.76, -52.34) * mm});
            skArc(sketch, "E19.3.4", {"start": v(-2.62, -10.76) * mm, "mid": v(0.23, -11.07) * mm, "end": v(3.07, -10.64) * mm});
            skLineSegment(sketch, "E19.3.5", {"start": v(3.07, -10.64) * mm, "end": v(14.94, -51.76) * mm});
            skArc(sketch, "E19.4.0", {"start": v(48.88, -33.22) * mm, "mid": v(49.6, -29.25) * mm, "end": v(47.16, -26.03) * mm});
            skArc(sketch, "E19.4.1", {"start": v(48.88, -33.22) * mm, "mid": v(42.66, -40.9) * mm, "end": v(35.24, -47.45) * mm});
            skArc(sketch, "E19.4.2", {"start": v(27.98, -46.03) * mm, "mid": v(31.3, -48.34) * mm, "end": v(35.24, -47.45) * mm});
            skLineSegment(sketch, "E19.4.3", {"start": v(5.75, -9.46) * mm, "end": v(27.98, -46.03) * mm});
            skArc(sketch, "E19.4.4", {"start": v(5.75, -9.46) * mm, "mid": v(8, -7.67) * mm, "end": v(9.7, -5.35) * mm});
            skLineSegment(sketch, "E19.4.5", {"start": v(9.7, -5.35) * mm, "end": v(47.16, -26.03) * mm});
            skArc(sketch, "E19.5.0", {"start": v(58.05, 11.07) * mm, "mid": v(55.76, 14.4) * mm, "end": v(51.76, 14.94) * mm});
            skArc(sketch, "E19.5.1", {"start": v(58.05, 11.07) * mm, "mid": v(59.09, 1.24) * mm, "end": v(58.47, -8.63) * mm});
            skArc(sketch, "E19.5.2", {"start": v(52.34, -12.76) * mm, "mid": v(56.31, -12.05) * mm, "end": v(58.47, -8.63) * mm});
            skLineSegment(sketch, "E19.5.3", {"start": v(10.76, -2.62) * mm, "end": v(52.34, -12.76) * mm});
            skArc(sketch, "E19.5.4", {"start": v(10.76, -2.62) * mm, "mid": v(11.07, 0.23) * mm, "end": v(10.64, 3.07) * mm});
            skLineSegment(sketch, "E19.5.5", {"start": v(10.64, 3.07) * mm, "end": v(51.76, 14.94) * mm});
            skArc(sketch, "E19.6.0", {"start": v(33.22, 48.88) * mm, "mid": v(29.25, 49.6) * mm, "end": v(26.03, 47.16) * mm});
            skArc(sketch, "E19.6.1", {"start": v(33.22, 48.88) * mm, "mid": v(40.9, 42.66) * mm, "end": v(47.45, 35.24) * mm});
            skArc(sketch, "E19.6.2", {"start": v(46.03, 27.98) * mm, "mid": v(48.34, 31.3) * mm, "end": v(47.45, 35.24) * mm});
            skLineSegment(sketch, "E19.6.3", {"start": v(9.46, 5.75) * mm, "end": v(46.03, 27.98) * mm});
            skArc(sketch, "E19.6.4", {"start": v(9.46, 5.75) * mm, "mid": v(7.67, 8) * mm, "end": v(5.35, 9.7) * mm});
            skLineSegment(sketch, "E19.6.5", {"start": v(5.35, 9.7) * mm, "end": v(26.03, 47.16) * mm});
            skArc(sketch, "E19.7.0", {"start": v(-11.07, 58.05) * mm, "mid": v(-14.4, 55.76) * mm, "end": v(-14.94, 51.76) * mm});
            skArc(sketch, "E19.7.1", {"start": v(-11.07, 58.05) * mm, "mid": v(-1.24, 59.09) * mm, "end": v(8.63, 58.47) * mm});
            skArc(sketch, "E19.7.2", {"start": v(12.76, 52.34) * mm, "mid": v(12.05, 56.31) * mm, "end": v(8.63, 58.47) * mm});
            skLineSegment(sketch, "E19.7.3", {"start": v(2.62, 10.76) * mm, "end": v(12.76, 52.34) * mm});
            skArc(sketch, "E19.7.4", {"start": v(2.62, 10.76) * mm, "mid": v(-0.23, 11.07) * mm, "end": v(-3.07, 10.64) * mm});
            skLineSegment(sketch, "E19.7.5", {"start": v(-3.07, 10.64) * mm, "end": v(-14.94, 51.76) * mm});
            skSolve(sketch);
        }
        {
            var Q0;
            Q0=makeQuery(id+"F0.imprint","IMPRINT",FACE,{"disambiguationData":[TD([[makeQuery(id+"F0.imprint","IMPRINT",EDGE,{"derivedFrom":sQuery(id+"F0.wireOp",EDGE,"E0")}),-1.0]])]});
            extrude(context, id + "F1", {"entities" : qUnion([Q0]), "endBound" : BoundingType.SYMMETRIC, "depth" : 10 * mm});
        }
        {
            var Q0;
            Q0 = qSketchRegion(id + "F0", true);
            extrude(context, id + "F2", {"entities" : qUnion([Q0]), "operationType" : NewBodyOperationType.ADD, "endBound" : BoundingType.SYMMETRIC, "depth" : 10 * mm});
        }
        {
            var Q0;
            Q0=makeQuery(id+"F1.opExtrude","CAP_EDGE",EDGE,{"disambiguationData":[OSD([sQuery(id+"F0.wireOp",EDGE,"E19.5.3")])],"isStart":false});
            var Q1;
            Q1=makeQuery(id+"F1.opExtrude","CAP_EDGE",EDGE,{"disambiguationData":[OSD([sQuery(id+"F0.wireOp",EDGE,"E19.5.5")])],"isStart":false});
            var Q2;
            Q2=makeQuery(id+"F1.opExtrude","CAP_EDGE",EDGE,{"disambiguationData":[OSD([sQuery(id+"F0.wireOp",EDGE,"E19.6.3")])],"isStart":false});
            var Q3;
            Q3=makeQuery(id+"F1.opExtrude","CAP_EDGE",EDGE,{"disambiguationData":[OSD([sQuery(id+"F0.wireOp",EDGE,"E19.6.5")])],"isStart":false});
            var Q4;
            Q4=makeQuery(id+"F1.opExtrude","CAP_EDGE",EDGE,{"disambiguationData":[OSD([sQuery(id+"F0.wireOp",EDGE,"E19.7.3")])],"isStart":false});
            var Q5;
            Q5=makeQuery(id+"F1.opExtrude","CAP_EDGE",EDGE,{"disambiguationData":[OSD([sQuery(id+"F0.wireOp",EDGE,"E19.7.5")])],"isStart":false});
            var Q6;
            Q6=makeQuery(id+"F1.opExtrude","CAP_EDGE",EDGE,{"disambiguationData":[OSD([sQuery(id+"F0.wireOp",EDGE,"E16.trimOffspring")])],"isStart":false});
            var Q7;
            {var subQ0=sQuery(id+"F0.wireOp",EDGE,"E19.7.5");var subQ1=sQuery(id+"F0.wireOp",EDGE,"E19.7.4");var subQ2=sQuery(id+"F0.wireOp",EDGE,"E19.7.3");var subQ3=sQuery(id+"F0.wireOp",EDGE,"E19.7.2");var subQ4=sQuery(id+"F0.wireOp",EDGE,"E19.7.1");var subQ5=sQuery(id+"F0.wireOp",EDGE,"E19.7.0");var subQ6=sQuery(id+"F0.wireOp",EDGE,"E19.6.5");var subQ7=sQuery(id+"F0.wireOp",EDGE,"E19.6.4");var subQ8=sQuery(id+"F0.wireOp",EDGE,"E19.6.3");var subQ9=sQuery(id+"F0.wireOp",EDGE,"E19.6.2");var subQ10=sQuery(id+"F0.wireOp",EDGE,"E19.6.1");var subQ11=sQuery(id+"F0.wireOp",EDGE,"E19.6.0");var subQ12=sQuery(id+"F0.wireOp",EDGE,"E19.5.5");var subQ13=sQuery(id+"F0.wireOp",EDGE,"E19.5.4");var subQ14=sQuery(id+"F0.wireOp",EDGE,"E19.5.3");var subQ15=sQuery(id+"F0.wireOp",EDGE,"E19.5.2");var subQ16=sQuery(id+"F0.wireOp",EDGE,"E19.5.1");var subQ17=sQuery(id+"F0.wireOp",EDGE,"E19.5.0");var subQ18=sQuery(id+"F0.wireOp",EDGE,"E19.4.5");var subQ19=sQuery(id+"F0.wireOp",EDGE,"E19.4.4");var subQ20=sQuery(id+"F0.wireOp",EDGE,"E19.4.3");var subQ21=sQuery(id+"F0.wireOp",EDGE,"E19.4.2");var subQ22=sQuery(id+"F0.wireOp",EDGE,"E19.4.1");var subQ23=sQuery(id+"F0.wireOp",EDGE,"E19.4.0");var subQ24=sQuery(id+"F0.wireOp",EDGE,"E19.3.5");var subQ25=sQuery(id+"F0.wireOp",EDGE,"E19.3.4");var subQ26=sQuery(id+"F0.wireOp",EDGE,"E19.3.3");var subQ27=sQuery(id+"F0.wireOp",EDGE,"E19.3.2");var subQ28=sQuery(id+"F0.wireOp",EDGE,"E19.3.1");var subQ29=sQuery(id+"F0.wireOp",EDGE,"E19.3.0");var subQ30=sQuery(id+"F0.wireOp",EDGE,"E19.2.5");var subQ31=sQuery(id+"F0.wireOp",EDGE,"E19.2.4");var subQ32=sQuery(id+"F0.wireOp",EDGE,"E19.2.3");var subQ33=sQuery(id+"F0.wireOp",EDGE,"E19.2.2");var subQ34=sQuery(id+"F0.wireOp",EDGE,"E19.2.1");var subQ35=sQuery(id+"F0.wireOp",EDGE,"E19.2.0");var subQ36=sQuery(id+"F0.wireOp",EDGE,"E19.1.5");var subQ37=sQuery(id+"F0.wireOp",EDGE,"E19.1.4");var subQ38=sQuery(id+"F0.wireOp",EDGE,"E19.1.3");var subQ39=sQuery(id+"F0.wireOp",EDGE,"E19.1.2");var subQ40=sQuery(id+"F0.wireOp",EDGE,"E19.1.1");var subQ41=sQuery(id+"F0.wireOp",EDGE,"E19.1.0");var subQ42=sQuery(id+"F0.wireOp",EDGE,"E18.filletArc");var subQ43=sQuery(id+"F0.wireOp",EDGE,"E17.filletArc");var subQ44=sQuery(id+"F0.wireOp",EDGE,"E16.trimOffspring");var subQ45=sQuery(id+"F0.wireOp",EDGE,"E15.trimOffspring");var subQ46=sQuery(id+"F0.wireOp",EDGE,"E14");var subQ47=sQuery(id+"F0.wireOp",EDGE,"E12.59.0");var subQ48=sQuery(id+"F0.wireOp",EDGE,"E12.58.0");var subQ49=sQuery(id+"F0.wireOp",EDGE,"E12.57.0");var subQ50=sQuery(id+"F0.wireOp",EDGE,"E12.56.0");var subQ51=sQuery(id+"F0.wireOp",EDGE,"E12.55.0");var subQ52=sQuery(id+"F0.wireOp",EDGE,"E12.54.0");var subQ53=sQuery(id+"F0.wireOp",EDGE,"E12.53.0");var subQ54=sQuery(id+"F0.wireOp",EDGE,"E12.52.0");var subQ55=sQuery(id+"F0.wireOp",EDGE,"E12.51.0");var subQ56=sQuery(id+"F0.wireOp",EDGE,"E12.50.0");var subQ57=sQuery(id+"F0.wireOp",EDGE,"E12.49.0");var subQ58=sQuery(id+"F0.wireOp",EDGE,"E12.48.0");var subQ59=sQuery(id+"F0.wireOp",EDGE,"E12.47.0");var subQ60=sQuery(id+"F0.wireOp",EDGE,"E12.46.0");var subQ61=sQuery(id+"F0.wireOp",EDGE,"E12.45.0");var subQ62=sQuery(id+"F0.wireOp",EDGE,"E12.44.0");var subQ63=sQuery(id+"F0.wireOp",EDGE,"E12.43.0");var subQ64=sQuery(id+"F0.wireOp",EDGE,"E12.42.0");var subQ65=sQuery(id+"F0.wireOp",EDGE,"E12.41.0");var subQ66=sQuery(id+"F0.wireOp",EDGE,"E12.40.0");var subQ67=sQuery(id+"F0.wireOp",EDGE,"E12.39.0");var subQ68=sQuery(id+"F0.wireOp",EDGE,"E12.38.0");var subQ69=sQuery(id+"F0.wireOp",EDGE,"E12.37.0");var subQ70=sQuery(id+"F0.wireOp",EDGE,"E12.36.0");var subQ71=sQuery(id+"F0.wireOp",EDGE,"E12.35.0");var subQ72=sQuery(id+"F0.wireOp",EDGE,"E12.34.0");var subQ73=sQuery(id+"F0.wireOp",EDGE,"E12.33.0");var subQ74=sQuery(id+"F0.wireOp",EDGE,"E12.32.0");var subQ75=sQuery(id+"F0.wireOp",EDGE,"E12.31.0");var subQ76=sQuery(id+"F0.wireOp",EDGE,"E12.30.0");var subQ77=sQuery(id+"F0.wireOp",EDGE,"E12.29.0");var subQ78=sQuery(id+"F0.wireOp",EDGE,"E12.28.0");var subQ79=sQuery(id+"F0.wireOp",EDGE,"E12.27.0");var subQ80=sQuery(id+"F0.wireOp",EDGE,"E12.26.0");var subQ81=sQuery(id+"F0.wireOp",EDGE,"E12.25.0");var subQ82=sQuery(id+"F0.wireOp",EDGE,"E12.24.0");var subQ83=sQuery(id+"F0.wireOp",EDGE,"E12.23.0");var subQ84=sQuery(id+"F0.wireOp",EDGE,"E12.22.0");var subQ85=sQuery(id+"F0.wireOp",EDGE,"E12.21.0");var subQ86=sQuery(id+"F0.wireOp",EDGE,"E12.20.0");var subQ87=sQuery(id+"F0.wireOp",EDGE,"E12.19.0");var subQ88=sQuery(id+"F0.wireOp",EDGE,"E12.18.0");var subQ89=sQuery(id+"F0.wireOp",EDGE,"E12.17.0");var subQ90=sQuery(id+"F0.wireOp",EDGE,"E12.16.0");var subQ91=sQuery(id+"F0.wireOp",EDGE,"E12.15.0");var subQ92=sQuery(id+"F0.wireOp",EDGE,"E12.14.0");var subQ93=sQuery(id+"F0.wireOp",EDGE,"E12.13.0");var subQ94=sQuery(id+"F0.wireOp",EDGE,"E12.12.0");var subQ95=sQuery(id+"F0.wireOp",EDGE,"E12.11.0");var subQ96=sQuery(id+"F0.wireOp",EDGE,"E12.10.0");var subQ97=sQuery(id+"F0.wireOp",EDGE,"E12.9.0");var subQ98=sQuery(id+"F0.wireOp",EDGE,"E12.8.0");var subQ99=sQuery(id+"F0.wireOp",EDGE,"E12.7.0");var subQ100=sQuery(id+"F0.wireOp",EDGE,"E12.6.0");var subQ101=sQuery(id+"F0.wireOp",EDGE,"E12.5.0");var subQ102=sQuery(id+"F0.wireOp",EDGE,"E12.4.0");var subQ103=sQuery(id+"F0.wireOp",EDGE,"E12.3.0");var subQ104=sQuery(id+"F0.wireOp",EDGE,"E12.2.0");var subQ105=sQuery(id+"F0.wireOp",EDGE,"E12.1.0");var subQ106=sQuery(id+"F0.wireOp",EDGE,"E11");var subQ107=sQuery(id+"F0.wireOp",EDGE,"E8");var subQ108=sQuery(id+"F0.wireOp",EDGE,"E7.59.5");var subQ109=sQuery(id+"F0.wireOp",EDGE,"E7.59.4");var subQ110=sQuery(id+"F0.wireOp",EDGE,"E7.59.3");var subQ111=sQuery(id+"F0.wireOp",EDGE,"E7.59.2");var subQ112=sQuery(id+"F0.wireOp",EDGE,"E7.59.1");var subQ113=sQuery(id+"F0.wireOp",EDGE,"E7.59.0");var subQ114=sQuery(id+"F0.wireOp",EDGE,"E7.58.5");var subQ115=sQuery(id+"F0.wireOp",EDGE,"E7.58.4");var subQ116=sQuery(id+"F0.wireOp",EDGE,"E7.58.3");var subQ117=sQuery(id+"F0.wireOp",EDGE,"E7.58.2");var subQ118=sQuery(id+"F0.wireOp",EDGE,"E7.58.1");var subQ119=sQuery(id+"F0.wireOp",EDGE,"E7.58.0");var subQ120=sQuery(id+"F0.wireOp",EDGE,"E7.57.5");var subQ121=sQuery(id+"F0.wireOp",EDGE,"E7.57.4");var subQ122=sQuery(id+"F0.wireOp",EDGE,"E7.57.3");var subQ123=sQuery(id+"F0.wireOp",EDGE,"E7.57.2");var subQ124=sQuery(id+"F0.wireOp",EDGE,"E7.57.1");var subQ125=sQuery(id+"F0.wireOp",EDGE,"E7.57.0");var subQ126=sQuery(id+"F0.wireOp",EDGE,"E7.56.5");var subQ127=sQuery(id+"F0.wireOp",EDGE,"E7.56.4");var subQ128=sQuery(id+"F0.wireOp",EDGE,"E7.56.3");var subQ129=sQuery(id+"F0.wireOp",EDGE,"E7.56.2");var subQ130=sQuery(id+"F0.wireOp",EDGE,"E7.56.1");var subQ131=sQuery(id+"F0.wireOp",EDGE,"E7.56.0");var subQ132=sQuery(id+"F0.wireOp",EDGE,"E7.55.5");var subQ133=sQuery(id+"F0.wireOp",EDGE,"E7.55.4");var subQ134=sQuery(id+"F0.wireOp",EDGE,"E7.55.3");var subQ135=sQuery(id+"F0.wireOp",EDGE,"E7.55.2");var subQ136=sQuery(id+"F0.wireOp",EDGE,"E7.55.1");var subQ137=sQuery(id+"F0.wireOp",EDGE,"E7.55.0");var subQ138=sQuery(id+"F0.wireOp",EDGE,"E7.54.5");var subQ139=sQuery(id+"F0.wireOp",EDGE,"E7.54.4");var subQ140=sQuery(id+"F0.wireOp",EDGE,"E7.54.3");var subQ141=sQuery(id+"F0.wireOp",EDGE,"E7.54.2");var subQ142=sQuery(id+"F0.wireOp",EDGE,"E7.54.1");var subQ143=sQuery(id+"F0.wireOp",EDGE,"E7.54.0");var subQ144=sQuery(id+"F0.wireOp",EDGE,"E7.53.5");var subQ145=sQuery(id+"F0.wireOp",EDGE,"E7.53.4");var subQ146=sQuery(id+"F0.wireOp",EDGE,"E7.53.3");var subQ147=sQuery(id+"F0.wireOp",EDGE,"E7.53.2");var subQ148=sQuery(id+"F0.wireOp",EDGE,"E7.53.1");var subQ149=sQuery(id+"F0.wireOp",EDGE,"E7.53.0");var subQ150=sQuery(id+"F0.wireOp",EDGE,"E7.52.5");var subQ151=sQuery(id+"F0.wireOp",EDGE,"E7.52.4");var subQ152=sQuery(id+"F0.wireOp",EDGE,"E7.52.3");var subQ153=sQuery(id+"F0.wireOp",EDGE,"E7.52.2");var subQ154=sQuery(id+"F0.wireOp",EDGE,"E7.52.1");var subQ155=sQuery(id+"F0.wireOp",EDGE,"E7.52.0");var subQ156=sQuery(id+"F0.wireOp",EDGE,"E7.51.5");var subQ157=sQuery(id+"F0.wireOp",EDGE,"E7.51.4");var subQ158=sQuery(id+"F0.wireOp",EDGE,"E7.51.3");var subQ159=sQuery(id+"F0.wireOp",EDGE,"E7.51.2");var subQ160=sQuery(id+"F0.wireOp",EDGE,"E7.51.1");var subQ161=sQuery(id+"F0.wireOp",EDGE,"E7.51.0");var subQ162=sQuery(id+"F0.wireOp",EDGE,"E7.50.5");var subQ163=sQuery(id+"F0.wireOp",EDGE,"E7.50.4");var subQ164=sQuery(id+"F0.wireOp",EDGE,"E7.50.3");var subQ165=sQuery(id+"F0.wireOp",EDGE,"E7.50.2");var subQ166=sQuery(id+"F0.wireOp",EDGE,"E7.50.1");var subQ167=sQuery(id+"F0.wireOp",EDGE,"E7.50.0");var subQ168=sQuery(id+"F0.wireOp",EDGE,"E7.49.5");var subQ169=sQuery(id+"F0.wireOp",EDGE,"E7.49.4");var subQ170=sQuery(id+"F0.wireOp",EDGE,"E7.49.3");var subQ171=sQuery(id+"F0.wireOp",EDGE,"E7.49.2");var subQ172=sQuery(id+"F0.wireOp",EDGE,"E7.49.1");var subQ173=sQuery(id+"F0.wireOp",EDGE,"E7.49.0");var subQ174=sQuery(id+"F0.wireOp",EDGE,"E7.48.5");var subQ175=sQuery(id+"F0.wireOp",EDGE,"E7.48.4");var subQ176=sQuery(id+"F0.wireOp",EDGE,"E7.48.3");var subQ177=sQuery(id+"F0.wireOp",EDGE,"E7.48.2");var subQ178=sQuery(id+"F0.wireOp",EDGE,"E7.48.1");var subQ179=sQuery(id+"F0.wireOp",EDGE,"E7.48.0");var subQ180=sQuery(id+"F0.wireOp",EDGE,"E7.47.5");var subQ181=sQuery(id+"F0.wireOp",EDGE,"E7.47.4");var subQ182=sQuery(id+"F0.wireOp",EDGE,"E7.47.3");var subQ183=sQuery(id+"F0.wireOp",EDGE,"E7.47.2");var subQ184=sQuery(id+"F0.wireOp",EDGE,"E7.47.1");var subQ185=sQuery(id+"F0.wireOp",EDGE,"E7.47.0");var subQ186=sQuery(id+"F0.wireOp",EDGE,"E7.46.5");var subQ187=sQuery(id+"F0.wireOp",EDGE,"E7.46.4");var subQ188=sQuery(id+"F0.wireOp",EDGE,"E7.46.3");var subQ189=sQuery(id+"F0.wireOp",EDGE,"E7.46.2");var subQ190=sQuery(id+"F0.wireOp",EDGE,"E7.46.1");var subQ191=sQuery(id+"F0.wireOp",EDGE,"E7.46.0");var subQ192=sQuery(id+"F0.wireOp",EDGE,"E7.45.5");var subQ193=sQuery(id+"F0.wireOp",EDGE,"E7.45.4");var subQ194=sQuery(id+"F0.wireOp",EDGE,"E7.45.3");var subQ195=sQuery(id+"F0.wireOp",EDGE,"E7.45.2");var subQ196=sQuery(id+"F0.wireOp",EDGE,"E7.45.1");var subQ197=sQuery(id+"F0.wireOp",EDGE,"E7.45.0");var subQ198=sQuery(id+"F0.wireOp",EDGE,"E7.44.5");var subQ199=sQuery(id+"F0.wireOp",EDGE,"E7.44.4");var subQ200=sQuery(id+"F0.wireOp",EDGE,"E7.44.3");var subQ201=sQuery(id+"F0.wireOp",EDGE,"E7.44.2");var subQ202=sQuery(id+"F0.wireOp",EDGE,"E7.44.1");var subQ203=sQuery(id+"F0.wireOp",EDGE,"E7.44.0");var subQ204=sQuery(id+"F0.wireOp",EDGE,"E7.43.5");var subQ205=sQuery(id+"F0.wireOp",EDGE,"E7.43.4");var subQ206=sQuery(id+"F0.wireOp",EDGE,"E7.43.3");var subQ207=sQuery(id+"F0.wireOp",EDGE,"E7.43.2");var subQ208=sQuery(id+"F0.wireOp",EDGE,"E7.43.1");var subQ209=sQuery(id+"F0.wireOp",EDGE,"E7.43.0");var subQ210=sQuery(id+"F0.wireOp",EDGE,"E7.42.5");var subQ211=sQuery(id+"F0.wireOp",EDGE,"E7.42.4");var subQ212=sQuery(id+"F0.wireOp",EDGE,"E7.42.3");var subQ213=sQuery(id+"F0.wireOp",EDGE,"E7.42.2");var subQ214=sQuery(id+"F0.wireOp",EDGE,"E7.42.1");var subQ215=sQuery(id+"F0.wireOp",EDGE,"E7.42.0");var subQ216=sQuery(id+"F0.wireOp",EDGE,"E7.41.5");var subQ217=sQuery(id+"F0.wireOp",EDGE,"E7.41.4");var subQ218=sQuery(id+"F0.wireOp",EDGE,"E7.41.3");var subQ219=sQuery(id+"F0.wireOp",EDGE,"E7.41.2");var subQ220=sQuery(id+"F0.wireOp",EDGE,"E7.41.1");var subQ221=sQuery(id+"F0.wireOp",EDGE,"E7.41.0");var subQ222=sQuery(id+"F0.wireOp",EDGE,"E7.40.5");var subQ223=sQuery(id+"F0.wireOp",EDGE,"E7.40.4");var subQ224=sQuery(id+"F0.wireOp",EDGE,"E7.40.3");var subQ225=sQuery(id+"F0.wireOp",EDGE,"E7.40.2");var subQ226=sQuery(id+"F0.wireOp",EDGE,"E7.40.1");var subQ227=sQuery(id+"F0.wireOp",EDGE,"E7.40.0");var subQ228=sQuery(id+"F0.wireOp",EDGE,"E7.39.5");var subQ229=sQuery(id+"F0.wireOp",EDGE,"E7.39.4");var subQ230=sQuery(id+"F0.wireOp",EDGE,"E7.39.3");var subQ231=sQuery(id+"F0.wireOp",EDGE,"E7.39.2");var subQ232=sQuery(id+"F0.wireOp",EDGE,"E7.39.1");var subQ233=sQuery(id+"F0.wireOp",EDGE,"E7.39.0");var subQ234=sQuery(id+"F0.wireOp",EDGE,"E7.38.5");var subQ235=sQuery(id+"F0.wireOp",EDGE,"E7.38.4");var subQ236=sQuery(id+"F0.wireOp",EDGE,"E7.38.3");var subQ237=sQuery(id+"F0.wireOp",EDGE,"E7.38.2");var subQ238=sQuery(id+"F0.wireOp",EDGE,"E7.38.1");var subQ239=sQuery(id+"F0.wireOp",EDGE,"E7.38.0");var subQ240=sQuery(id+"F0.wireOp",EDGE,"E7.37.5");var subQ241=sQuery(id+"F0.wireOp",EDGE,"E7.37.4");var subQ242=sQuery(id+"F0.wireOp",EDGE,"E7.37.3");var subQ243=sQuery(id+"F0.wireOp",EDGE,"E7.37.2");var subQ244=sQuery(id+"F0.wireOp",EDGE,"E7.37.1");var subQ245=sQuery(id+"F0.wireOp",EDGE,"E7.37.0");var subQ246=sQuery(id+"F0.wireOp",EDGE,"E7.36.5");var subQ247=sQuery(id+"F0.wireOp",EDGE,"E7.36.4");var subQ248=sQuery(id+"F0.wireOp",EDGE,"E7.36.3");var subQ249=sQuery(id+"F0.wireOp",EDGE,"E7.36.2");var subQ250=sQuery(id+"F0.wireOp",EDGE,"E7.36.1");var subQ251=sQuery(id+"F0.wireOp",EDGE,"E7.36.0");var subQ252=sQuery(id+"F0.wireOp",EDGE,"E7.35.5");var subQ253=sQuery(id+"F0.wireOp",EDGE,"E7.35.4");var subQ254=sQuery(id+"F0.wireOp",EDGE,"E7.35.3");var subQ255=sQuery(id+"F0.wireOp",EDGE,"E7.35.2");var subQ256=sQuery(id+"F0.wireOp",EDGE,"E7.35.1");var subQ257=sQuery(id+"F0.wireOp",EDGE,"E7.35.0");var subQ258=sQuery(id+"F0.wireOp",EDGE,"E7.34.5");var subQ259=sQuery(id+"F0.wireOp",EDGE,"E7.34.4");var subQ260=sQuery(id+"F0.wireOp",EDGE,"E7.34.3");var subQ261=sQuery(id+"F0.wireOp",EDGE,"E7.34.2");var subQ262=sQuery(id+"F0.wireOp",EDGE,"E7.34.1");var subQ263=sQuery(id+"F0.wireOp",EDGE,"E7.34.0");var subQ264=sQuery(id+"F0.wireOp",EDGE,"E7.33.5");var subQ265=sQuery(id+"F0.wireOp",EDGE,"E7.33.4");var subQ266=sQuery(id+"F0.wireOp",EDGE,"E7.33.3");var subQ267=sQuery(id+"F0.wireOp",EDGE,"E7.33.2");var subQ268=sQuery(id+"F0.wireOp",EDGE,"E7.33.1");var subQ269=sQuery(id+"F0.wireOp",EDGE,"E7.33.0");var subQ270=sQuery(id+"F0.wireOp",EDGE,"E7.32.5");var subQ271=sQuery(id+"F0.wireOp",EDGE,"E7.32.4");var subQ272=sQuery(id+"F0.wireOp",EDGE,"E7.32.3");var subQ273=sQuery(id+"F0.wireOp",EDGE,"E7.32.2");var subQ274=sQuery(id+"F0.wireOp",EDGE,"E7.32.1");var subQ275=sQuery(id+"F0.wireOp",EDGE,"E7.32.0");var subQ276=sQuery(id+"F0.wireOp",EDGE,"E7.31.5");var subQ277=sQuery(id+"F0.wireOp",EDGE,"E7.31.4");var subQ278=sQuery(id+"F0.wireOp",EDGE,"E7.31.3");var subQ279=sQuery(id+"F0.wireOp",EDGE,"E7.31.2");var subQ280=sQuery(id+"F0.wireOp",EDGE,"E7.31.1");var subQ281=sQuery(id+"F0.wireOp",EDGE,"E7.31.0");var subQ282=sQuery(id+"F0.wireOp",EDGE,"E7.30.5");var subQ283=sQuery(id+"F0.wireOp",EDGE,"E7.30.4");var subQ284=sQuery(id+"F0.wireOp",EDGE,"E7.30.3");var subQ285=sQuery(id+"F0.wireOp",EDGE,"E7.30.2");var subQ286=sQuery(id+"F0.wireOp",EDGE,"E7.30.1");var subQ287=sQuery(id+"F0.wireOp",EDGE,"E7.30.0");var subQ288=sQuery(id+"F0.wireOp",EDGE,"E7.29.5");var subQ289=sQuery(id+"F0.wireOp",EDGE,"E7.29.4");var subQ290=sQuery(id+"F0.wireOp",EDGE,"E7.29.3");var subQ291=sQuery(id+"F0.wireOp",EDGE,"E7.29.2");var subQ292=sQuery(id+"F0.wireOp",EDGE,"E7.29.1");var subQ293=sQuery(id+"F0.wireOp",EDGE,"E7.29.0");var subQ294=sQuery(id+"F0.wireOp",EDGE,"E7.28.5");var subQ295=sQuery(id+"F0.wireOp",EDGE,"E7.28.4");var subQ296=sQuery(id+"F0.wireOp",EDGE,"E7.28.3");var subQ297=sQuery(id+"F0.wireOp",EDGE,"E7.28.2");var subQ298=sQuery(id+"F0.wireOp",EDGE,"E7.28.1");var subQ299=sQuery(id+"F0.wireOp",EDGE,"E7.28.0");var subQ300=sQuery(id+"F0.wireOp",EDGE,"E7.27.5");var subQ301=sQuery(id+"F0.wireOp",EDGE,"E7.27.4");var subQ302=sQuery(id+"F0.wireOp",EDGE,"E7.27.3");var subQ303=sQuery(id+"F0.wireOp",EDGE,"E7.27.2");var subQ304=sQuery(id+"F0.wireOp",EDGE,"E7.27.1");var subQ305=sQuery(id+"F0.wireOp",EDGE,"E7.27.0");var subQ306=sQuery(id+"F0.wireOp",EDGE,"E7.26.5");var subQ307=sQuery(id+"F0.wireOp",EDGE,"E7.26.4");var subQ308=sQuery(id+"F0.wireOp",EDGE,"E7.26.3");var subQ309=sQuery(id+"F0.wireOp",EDGE,"E7.26.2");var subQ310=sQuery(id+"F0.wireOp",EDGE,"E7.26.1");var subQ311=sQuery(id+"F0.wireOp",EDGE,"E7.26.0");var subQ312=sQuery(id+"F0.wireOp",EDGE,"E7.25.5");var subQ313=sQuery(id+"F0.wireOp",EDGE,"E7.25.4");var subQ314=sQuery(id+"F0.wireOp",EDGE,"E7.25.3");var subQ315=sQuery(id+"F0.wireOp",EDGE,"E7.25.2");var subQ316=sQuery(id+"F0.wireOp",EDGE,"E7.25.1");var subQ317=sQuery(id+"F0.wireOp",EDGE,"E7.25.0");var subQ318=sQuery(id+"F0.wireOp",EDGE,"E7.24.5");var subQ319=sQuery(id+"F0.wireOp",EDGE,"E7.24.4");var subQ320=sQuery(id+"F0.wireOp",EDGE,"E7.24.3");var subQ321=sQuery(id+"F0.wireOp",EDGE,"E7.24.2");var subQ322=sQuery(id+"F0.wireOp",EDGE,"E7.24.1");var subQ323=sQuery(id+"F0.wireOp",EDGE,"E7.24.0");var subQ324=sQuery(id+"F0.wireOp",EDGE,"E7.23.5");var subQ325=sQuery(id+"F0.wireOp",EDGE,"E7.23.4");var subQ326=sQuery(id+"F0.wireOp",EDGE,"E7.23.3");var subQ327=sQuery(id+"F0.wireOp",EDGE,"E7.23.2");var subQ328=sQuery(id+"F0.wireOp",EDGE,"E7.23.1");var subQ329=sQuery(id+"F0.wireOp",EDGE,"E7.23.0");var subQ330=sQuery(id+"F0.wireOp",EDGE,"E7.22.5");var subQ331=sQuery(id+"F0.wireOp",EDGE,"E7.22.4");var subQ332=sQuery(id+"F0.wireOp",EDGE,"E7.22.3");var subQ333=sQuery(id+"F0.wireOp",EDGE,"E7.22.2");var subQ334=sQuery(id+"F0.wireOp",EDGE,"E7.22.1");var subQ335=sQuery(id+"F0.wireOp",EDGE,"E7.22.0");var subQ336=sQuery(id+"F0.wireOp",EDGE,"E7.21.5");var subQ337=sQuery(id+"F0.wireOp",EDGE,"E7.21.4");var subQ338=sQuery(id+"F0.wireOp",EDGE,"E7.21.3");var subQ339=sQuery(id+"F0.wireOp",EDGE,"E7.21.2");var subQ340=sQuery(id+"F0.wireOp",EDGE,"E7.21.1");var subQ341=sQuery(id+"F0.wireOp",EDGE,"E7.21.0");var subQ342=sQuery(id+"F0.wireOp",EDGE,"E7.20.5");var subQ343=sQuery(id+"F0.wireOp",EDGE,"E7.20.4");var subQ344=sQuery(id+"F0.wireOp",EDGE,"E7.20.3");var subQ345=sQuery(id+"F0.wireOp",EDGE,"E7.20.2");var subQ346=sQuery(id+"F0.wireOp",EDGE,"E7.20.1");var subQ347=sQuery(id+"F0.wireOp",EDGE,"E7.20.0");var subQ348=sQuery(id+"F0.wireOp",EDGE,"E7.19.5");var subQ349=sQuery(id+"F0.wireOp",EDGE,"E7.19.4");var subQ350=sQuery(id+"F0.wireOp",EDGE,"E7.19.3");var subQ351=sQuery(id+"F0.wireOp",EDGE,"E7.19.2");var subQ352=sQuery(id+"F0.wireOp",EDGE,"E7.19.1");var subQ353=sQuery(id+"F0.wireOp",EDGE,"E7.19.0");var subQ354=sQuery(id+"F0.wireOp",EDGE,"E7.18.5");var subQ355=sQuery(id+"F0.wireOp",EDGE,"E7.18.4");var subQ356=sQuery(id+"F0.wireOp",EDGE,"E7.18.3");var subQ357=sQuery(id+"F0.wireOp",EDGE,"E7.18.2");var subQ358=sQuery(id+"F0.wireOp",EDGE,"E7.18.1");var subQ359=sQuery(id+"F0.wireOp",EDGE,"E7.18.0");var subQ360=sQuery(id+"F0.wireOp",EDGE,"E7.17.5");var subQ361=sQuery(id+"F0.wireOp",EDGE,"E7.17.4");var subQ362=sQuery(id+"F0.wireOp",EDGE,"E7.17.3");var subQ363=sQuery(id+"F0.wireOp",EDGE,"E7.17.2");var subQ364=sQuery(id+"F0.wireOp",EDGE,"E7.17.1");var subQ365=sQuery(id+"F0.wireOp",EDGE,"E7.17.0");var subQ366=sQuery(id+"F0.wireOp",EDGE,"E7.16.5");var subQ367=sQuery(id+"F0.wireOp",EDGE,"E7.16.4");var subQ368=sQuery(id+"F0.wireOp",EDGE,"E7.16.3");var subQ369=sQuery(id+"F0.wireOp",EDGE,"E7.16.2");var subQ370=sQuery(id+"F0.wireOp",EDGE,"E7.16.1");var subQ371=sQuery(id+"F0.wireOp",EDGE,"E7.16.0");var subQ372=sQuery(id+"F0.wireOp",EDGE,"E7.15.5");var subQ373=sQuery(id+"F0.wireOp",EDGE,"E7.15.4");var subQ374=sQuery(id+"F0.wireOp",EDGE,"E7.15.3");var subQ375=sQuery(id+"F0.wireOp",EDGE,"E7.15.2");var subQ376=sQuery(id+"F0.wireOp",EDGE,"E7.15.1");var subQ377=sQuery(id+"F0.wireOp",EDGE,"E7.15.0");var subQ378=sQuery(id+"F0.wireOp",EDGE,"E7.14.5");var subQ379=sQuery(id+"F0.wireOp",EDGE,"E7.14.4");var subQ380=sQuery(id+"F0.wireOp",EDGE,"E7.14.3");var subQ381=sQuery(id+"F0.wireOp",EDGE,"E7.14.2");var subQ382=sQuery(id+"F0.wireOp",EDGE,"E7.14.1");var subQ383=sQuery(id+"F0.wireOp",EDGE,"E7.14.0");var subQ384=sQuery(id+"F0.wireOp",EDGE,"E7.13.5");var subQ385=sQuery(id+"F0.wireOp",EDGE,"E7.13.4");var subQ386=sQuery(id+"F0.wireOp",EDGE,"E7.13.3");var subQ387=sQuery(id+"F0.wireOp",EDGE,"E7.13.2");var subQ388=sQuery(id+"F0.wireOp",EDGE,"E7.13.1");var subQ389=sQuery(id+"F0.wireOp",EDGE,"E7.13.0");var subQ390=sQuery(id+"F0.wireOp",EDGE,"E7.12.5");var subQ391=sQuery(id+"F0.wireOp",EDGE,"E7.12.4");var subQ392=sQuery(id+"F0.wireOp",EDGE,"E7.12.3");var subQ393=sQuery(id+"F0.wireOp",EDGE,"E7.12.2");var subQ394=sQuery(id+"F0.wireOp",EDGE,"E7.12.1");var subQ395=sQuery(id+"F0.wireOp",EDGE,"E7.12.0");var subQ396=sQuery(id+"F0.wireOp",EDGE,"E7.11.5");var subQ397=sQuery(id+"F0.wireOp",EDGE,"E7.11.4");var subQ398=sQuery(id+"F0.wireOp",EDGE,"E7.11.3");var subQ399=sQuery(id+"F0.wireOp",EDGE,"E7.11.2");var subQ400=sQuery(id+"F0.wireOp",EDGE,"E7.11.1");var subQ401=sQuery(id+"F0.wireOp",EDGE,"E7.11.0");var subQ402=sQuery(id+"F0.wireOp",EDGE,"E7.10.5");var subQ403=sQuery(id+"F0.wireOp",EDGE,"E7.10.4");var subQ404=sQuery(id+"F0.wireOp",EDGE,"E7.10.3");var subQ405=sQuery(id+"F0.wireOp",EDGE,"E7.10.2");var subQ406=sQuery(id+"F0.wireOp",EDGE,"E7.10.1");var subQ407=sQuery(id+"F0.wireOp",EDGE,"E7.10.0");var subQ408=sQuery(id+"F0.wireOp",EDGE,"E7.9.5");var subQ409=sQuery(id+"F0.wireOp",EDGE,"E7.9.4");var subQ410=sQuery(id+"F0.wireOp",EDGE,"E7.9.3");var subQ411=sQuery(id+"F0.wireOp",EDGE,"E7.9.2");var subQ412=sQuery(id+"F0.wireOp",EDGE,"E7.9.1");var subQ413=sQuery(id+"F0.wireOp",EDGE,"E7.9.0");var subQ414=sQuery(id+"F0.wireOp",EDGE,"E7.8.5");var subQ415=sQuery(id+"F0.wireOp",EDGE,"E7.8.4");var subQ416=sQuery(id+"F0.wireOp",EDGE,"E7.8.3");var subQ417=sQuery(id+"F0.wireOp",EDGE,"E7.8.2");var subQ418=sQuery(id+"F0.wireOp",EDGE,"E7.8.1");var subQ419=sQuery(id+"F0.wireOp",EDGE,"E7.8.0");var subQ420=sQuery(id+"F0.wireOp",EDGE,"E7.7.5");var subQ421=sQuery(id+"F0.wireOp",EDGE,"E7.7.4");var subQ422=sQuery(id+"F0.wireOp",EDGE,"E7.7.3");var subQ423=sQuery(id+"F0.wireOp",EDGE,"E7.7.2");var subQ424=sQuery(id+"F0.wireOp",EDGE,"E7.7.1");var subQ425=sQuery(id+"F0.wireOp",EDGE,"E7.7.0");var subQ426=sQuery(id+"F0.wireOp",EDGE,"E7.6.5");var subQ427=sQuery(id+"F0.wireOp",EDGE,"E7.6.4");var subQ428=sQuery(id+"F0.wireOp",EDGE,"E7.6.3");var subQ429=sQuery(id+"F0.wireOp",EDGE,"E7.6.2");var subQ430=sQuery(id+"F0.wireOp",EDGE,"E7.6.1");var subQ431=sQuery(id+"F0.wireOp",EDGE,"E7.6.0");var subQ432=sQuery(id+"F0.wireOp",EDGE,"E7.5.5");var subQ433=sQuery(id+"F0.wireOp",EDGE,"E7.5.4");var subQ434=sQuery(id+"F0.wireOp",EDGE,"E7.5.3");var subQ435=sQuery(id+"F0.wireOp",EDGE,"E7.5.2");var subQ436=sQuery(id+"F0.wireOp",EDGE,"E7.5.1");var subQ437=sQuery(id+"F0.wireOp",EDGE,"E7.5.0");var subQ438=sQuery(id+"F0.wireOp",EDGE,"E7.4.5");var subQ439=sQuery(id+"F0.wireOp",EDGE,"E7.4.4");var subQ440=sQuery(id+"F0.wireOp",EDGE,"E7.4.3");var subQ441=sQuery(id+"F0.wireOp",EDGE,"E7.4.2");var subQ442=sQuery(id+"F0.wireOp",EDGE,"E7.4.1");var subQ443=sQuery(id+"F0.wireOp",EDGE,"E7.4.0");var subQ444=sQuery(id+"F0.wireOp",EDGE,"E7.3.5");var subQ445=sQuery(id+"F0.wireOp",EDGE,"E7.3.4");var subQ446=sQuery(id+"F0.wireOp",EDGE,"E7.3.3");var subQ447=sQuery(id+"F0.wireOp",EDGE,"E7.3.2");var subQ448=sQuery(id+"F0.wireOp",EDGE,"E7.3.1");var subQ449=sQuery(id+"F0.wireOp",EDGE,"E7.3.0");var subQ450=sQuery(id+"F0.wireOp",EDGE,"E7.2.5");var subQ451=sQuery(id+"F0.wireOp",EDGE,"E7.2.4");var subQ452=sQuery(id+"F0.wireOp",EDGE,"E7.2.3");var subQ453=sQuery(id+"F0.wireOp",EDGE,"E7.2.2");var subQ454=sQuery(id+"F0.wireOp",EDGE,"E7.2.1");var subQ455=sQuery(id+"F0.wireOp",EDGE,"E7.2.0");var subQ456=sQuery(id+"F0.wireOp",EDGE,"E7.1.5");var subQ457=sQuery(id+"F0.wireOp",EDGE,"E7.1.4");var subQ458=sQuery(id+"F0.wireOp",EDGE,"E7.1.3");var subQ459=sQuery(id+"F0.wireOp",EDGE,"E7.1.2");var subQ460=sQuery(id+"F0.wireOp",EDGE,"E7.1.1");var subQ461=sQuery(id+"F0.wireOp",EDGE,"E7.1.0");var subQ462=sQuery(id+"F0.wireOp",EDGE,"E6.MirrorCS");var subQ463=sQuery(id+"F0.wireOp",EDGE,"E5.MirrorCS");var subQ464=sQuery(id+"F0.wireOp",EDGE,"E4.MirrorCS");var subQ465=sQuery(id+"F0.wireOp",EDGE,"E3");var subQ466=sQuery(id+"F0.wireOp",EDGE,"E2");var subQ467=sQuery(id+"F0.wireOp",EDGE,"E1");var subQ468=sQuery(id+"F0.wireOp",EDGE,"E0");Q7=makeQuery(id+"F2.boolean.opBoolean","MERGE",FACE,{"derivedFrom":[makeQuery(id+"F1.opExtrude","CAP_FACE",FACE,{"disambiguationData":[OSD([subQ468,subQ467,subQ466,subQ465,subQ464,subQ463,subQ462,subQ461,subQ460,subQ459,subQ458,subQ457,subQ456,subQ455,subQ454,subQ453,subQ452,subQ451,subQ450,subQ449,subQ448,subQ447,subQ446,subQ445,subQ444,subQ443,subQ442,subQ441,subQ440,subQ439,subQ438,subQ437,subQ436,subQ435,subQ434,subQ433,subQ432,subQ431,subQ430,subQ429,subQ428,subQ427,subQ426,subQ425,subQ424,subQ423,subQ422,subQ421,subQ420,subQ419,subQ418,subQ417,subQ416,subQ415,subQ414,subQ413,subQ412,subQ411,subQ410,subQ409,subQ408,subQ407,subQ406,subQ405,subQ404,subQ403,subQ402,subQ401,subQ400,subQ399,subQ398,subQ397,subQ396,subQ395,subQ394,subQ393,subQ392,subQ391,subQ390,subQ389,subQ388,subQ387,subQ386,subQ385,subQ384,subQ383,subQ382,subQ381,subQ380,subQ379,subQ378,subQ377,subQ376,subQ375,subQ374,subQ373,subQ372,subQ371,subQ370,subQ369,subQ368,subQ367,subQ366,subQ365,subQ364,subQ363,subQ362,subQ361,subQ360,subQ359,subQ358,subQ357,subQ356,subQ355,subQ354,subQ353,subQ352,subQ351,subQ350,subQ349,subQ348,subQ347,subQ346,subQ345,subQ344,subQ343,subQ342,subQ341,subQ340,subQ339,subQ338,subQ337,subQ336,subQ335,subQ334,subQ333,subQ332,subQ331,subQ330,subQ329,subQ328,subQ327,subQ326,subQ325,subQ324,subQ323,subQ322,subQ321,subQ320,subQ319,subQ318,subQ317,subQ316,subQ315,subQ314,subQ313,subQ312,subQ311,subQ310,subQ309,subQ308,subQ307,subQ306,subQ305,subQ304,subQ303,subQ302,subQ301,subQ300,subQ299,subQ298,subQ297,subQ296,subQ295,subQ294,subQ293,subQ292,subQ291,subQ290,subQ289,subQ288,subQ287,subQ286,subQ285,subQ284,subQ283,subQ282,subQ281,subQ280,subQ279,subQ278,subQ277,subQ276,subQ275,subQ274,subQ273,subQ272,subQ271,subQ270,subQ269,subQ268,subQ267,subQ266,subQ265,subQ264,subQ263,subQ262,subQ261,subQ260,subQ259,subQ258,subQ257,subQ256,subQ255,subQ254,subQ253,subQ252,subQ251,subQ250,subQ249,subQ248,subQ247,subQ246,subQ245,subQ244,subQ243,subQ242,subQ241,subQ240,subQ239,subQ238,subQ237,subQ236,subQ235,subQ234,subQ233,subQ232,subQ231,subQ230,subQ229,subQ228,subQ227,subQ226,subQ225,subQ224,subQ223,subQ222,subQ221,subQ220,subQ219,subQ218,subQ217,subQ216,subQ215,subQ214,subQ213,subQ212,subQ211,subQ210,subQ209,subQ208,subQ207,subQ206,subQ205,subQ204,subQ203,subQ202,subQ201,subQ200,subQ199,subQ198,subQ197,subQ196,subQ195,subQ194,subQ193,subQ192,subQ191,subQ190,subQ189,subQ188,subQ187,subQ186,subQ185,subQ184,subQ183,subQ182,subQ181,subQ180,subQ179,subQ178,subQ177,subQ176,subQ175,subQ174,subQ173,subQ172,subQ171,subQ170,subQ169,subQ168,subQ167,subQ166,subQ165,subQ164,subQ163,subQ162,subQ161,subQ160,subQ159,subQ158,subQ157,subQ156,subQ155,subQ154,subQ153,subQ152,subQ151,subQ150,subQ149,subQ148,subQ147,subQ146,subQ145,subQ144,subQ143,subQ142,subQ141,subQ140,subQ139,subQ138,subQ137,subQ136,subQ135,subQ134,subQ133,subQ132,subQ131,subQ130,subQ129,subQ128,subQ127,subQ126,subQ125,subQ124,subQ123,subQ122,subQ121,subQ120,subQ119,subQ118,subQ117,subQ116,subQ115,subQ114,subQ113,subQ112,subQ111,subQ110,subQ109,subQ108,subQ107,subQ106,subQ105,subQ104,subQ103,subQ102,subQ101,subQ100,subQ99,subQ98,subQ97,subQ96,subQ95,subQ94,subQ93,subQ92,subQ91,subQ90,subQ89,subQ88,subQ87,subQ86,subQ85,subQ84,subQ83,subQ82,subQ81,subQ80,subQ79,subQ78,subQ77,subQ76,subQ75,subQ74,subQ73,subQ72,subQ71,subQ70,subQ69,subQ68,subQ67,subQ66,subQ65,subQ64,subQ63,subQ62,subQ61,subQ60,subQ59,subQ58,subQ57,subQ56,subQ55,subQ54,subQ53,subQ52,subQ51,subQ50,subQ49,subQ48,subQ47,subQ46,subQ45,subQ44,subQ43,subQ42,subQ41,subQ40,subQ39,subQ38,subQ37,subQ36,subQ35,subQ34,subQ33,subQ32,subQ31,subQ30,subQ29,subQ28,subQ27,subQ26,subQ25,subQ24,subQ23,subQ22,subQ21,subQ20,subQ19,subQ18,subQ17,subQ16,subQ15,subQ14,subQ13,subQ12,subQ11,subQ10,subQ9,subQ8,subQ7,subQ6,subQ5,subQ4,subQ3,subQ2,subQ1,subQ0])],"isStart":false}),makeQuery(id+"F2.opExtrude","CAP_FACE",FACE,{"disambiguationData":[OSD([subQ468,subQ467,subQ466,subQ465,subQ464,subQ463,subQ462,subQ461,subQ460,subQ459,subQ458,subQ457,subQ456,subQ455,subQ454,subQ453,subQ452,subQ451,subQ450,subQ449,subQ448,subQ447,subQ446,subQ445,subQ444,subQ443,subQ442,subQ441,subQ440,subQ439,subQ438,subQ437,subQ436,subQ435,subQ434,subQ433,subQ432,subQ431,subQ430,subQ429,subQ428,subQ427,subQ426,subQ425,subQ424,subQ423,subQ422,subQ421,subQ420,subQ419,subQ418,subQ417,subQ416,subQ415,subQ414,subQ413,subQ412,subQ411,subQ410,subQ409,subQ408,subQ407,subQ406,subQ405,subQ404,subQ403,subQ402,subQ401,subQ400,subQ399,subQ398,subQ397,subQ396,subQ395,subQ394,subQ393,subQ392,subQ391,subQ390,subQ389,subQ388,subQ387,subQ386,subQ385,subQ384,subQ383,subQ382,subQ381,subQ380,subQ379,subQ378,subQ377,subQ376,subQ375,subQ374,subQ373,subQ372,subQ371,subQ370,subQ369,subQ368,subQ367,subQ366,subQ365,subQ364,subQ363,subQ362,subQ361,subQ360,subQ359,subQ358,subQ357,subQ356,subQ355,subQ354,subQ353,subQ352,subQ351,subQ350,subQ349,subQ348,subQ347,subQ346,subQ345,subQ344,subQ343,subQ342,subQ341,subQ340,subQ339,subQ338,subQ337,subQ336,subQ335,subQ334,subQ333,subQ332,subQ331,subQ330,subQ329,subQ328,subQ327,subQ326,subQ325,subQ324,subQ323,subQ322,subQ321,subQ320,subQ319,subQ318,subQ317,subQ316,subQ315,subQ314,subQ313,subQ312,subQ311,subQ310,subQ309,subQ308,subQ307,subQ306,subQ305,subQ304,subQ303,subQ302,subQ301,subQ300,subQ299,subQ298,subQ297,subQ296,subQ295,subQ294,subQ293,subQ292,subQ291,subQ290,subQ289,subQ288,subQ287,subQ286,subQ285,subQ284,subQ283,subQ282,subQ281,subQ280,subQ279,subQ278,subQ277,subQ276,subQ275,subQ274,subQ273,subQ272,subQ271,subQ270,subQ269,subQ268,subQ267,subQ266,subQ265,subQ264,subQ263,subQ262,subQ261,subQ260,subQ259,subQ258,subQ257,subQ256,subQ255,subQ254,subQ253,subQ252,subQ251,subQ250,subQ249,subQ248,subQ247,subQ246,subQ245,subQ244,subQ243,subQ242,subQ241,subQ240,subQ239,subQ238,subQ237,subQ236,subQ235,subQ234,subQ233,subQ232,subQ231,subQ230,subQ229,subQ228,subQ227,subQ226,subQ225,subQ224,subQ223,subQ222,subQ221,subQ220,subQ219,subQ218,subQ217,subQ216,subQ215,subQ214,subQ213,subQ212,subQ211,subQ210,subQ209,subQ208,subQ207,subQ206,subQ205,subQ204,subQ203,subQ202,subQ201,subQ200,subQ199,subQ198,subQ197,subQ196,subQ195,subQ194,subQ193,subQ192,subQ191,subQ190,subQ189,subQ188,subQ187,subQ186,subQ185,subQ184,subQ183,subQ182,subQ181,subQ180,subQ179,subQ178,subQ177,subQ176,subQ175,subQ174,subQ173,subQ172,subQ171,subQ170,subQ169,subQ168,subQ167,subQ166,subQ165,subQ164,subQ163,subQ162,subQ161,subQ160,subQ159,subQ158,subQ157,subQ156,subQ155,subQ154,subQ153,subQ152,subQ151,subQ150,subQ149,subQ148,subQ147,subQ146,subQ145,subQ144,subQ143,subQ142,subQ141,subQ140,subQ139,subQ138,subQ137,subQ136,subQ135,subQ134,subQ133,subQ132,subQ131,subQ130,subQ129,subQ128,subQ127,subQ126,subQ125,subQ124,subQ123,subQ122,subQ121,subQ120,subQ119,subQ118,subQ117,subQ116,subQ115,subQ114,subQ113,subQ112,subQ111,subQ110,subQ109,subQ108,subQ107,subQ106,subQ105,subQ104,subQ103,subQ102,subQ101,subQ100,subQ99,subQ98,subQ97,subQ96,subQ95,subQ94,subQ93,subQ92,subQ91,subQ90,subQ89,subQ88,subQ87,subQ86,subQ85,subQ84,subQ83,subQ82,subQ81,subQ80,subQ79,subQ78,subQ77,subQ76,subQ75,subQ74,subQ73,subQ72,subQ71,subQ70,subQ69,subQ68,subQ67,subQ66,subQ65,subQ64,subQ63,subQ62,subQ61,subQ60,subQ59,subQ58,subQ57,subQ56,subQ55,subQ54,subQ53,subQ52,subQ51,subQ50,subQ49,subQ48,subQ47,subQ46,subQ45,subQ44,subQ43,subQ42,subQ41,subQ40,subQ39,subQ38,subQ37,subQ36,subQ35,subQ34,subQ33,subQ32,subQ31,subQ30,subQ29,subQ28,subQ27,subQ26,subQ25,subQ24,subQ23,subQ22,subQ21,subQ20,subQ19,subQ18,subQ17,subQ16,subQ15,subQ14,subQ13,subQ12,subQ11,subQ10,subQ9,subQ8,subQ7,subQ6,subQ5,subQ4,subQ3,subQ2,subQ1,subQ0])],"isStart":false})]});}
            var Q8;
            {var subQ0=sQuery(id+"F0.wireOp",EDGE,"E19.7.5");var subQ1=sQuery(id+"F0.wireOp",EDGE,"E19.7.4");var subQ2=sQuery(id+"F0.wireOp",EDGE,"E19.7.3");var subQ3=sQuery(id+"F0.wireOp",EDGE,"E19.7.2");var subQ4=sQuery(id+"F0.wireOp",EDGE,"E19.7.1");var subQ5=sQuery(id+"F0.wireOp",EDGE,"E19.7.0");var subQ6=sQuery(id+"F0.wireOp",EDGE,"E19.6.5");var subQ7=sQuery(id+"F0.wireOp",EDGE,"E19.6.4");var subQ8=sQuery(id+"F0.wireOp",EDGE,"E19.6.3");var subQ9=sQuery(id+"F0.wireOp",EDGE,"E19.6.2");var subQ10=sQuery(id+"F0.wireOp",EDGE,"E19.6.1");var subQ11=sQuery(id+"F0.wireOp",EDGE,"E19.6.0");var subQ12=sQuery(id+"F0.wireOp",EDGE,"E19.5.5");var subQ13=sQuery(id+"F0.wireOp",EDGE,"E19.5.4");var subQ14=sQuery(id+"F0.wireOp",EDGE,"E19.5.3");var subQ15=sQuery(id+"F0.wireOp",EDGE,"E19.5.2");var subQ16=sQuery(id+"F0.wireOp",EDGE,"E19.5.1");var subQ17=sQuery(id+"F0.wireOp",EDGE,"E19.5.0");var subQ18=sQuery(id+"F0.wireOp",EDGE,"E19.4.5");var subQ19=sQuery(id+"F0.wireOp",EDGE,"E19.4.4");var subQ20=sQuery(id+"F0.wireOp",EDGE,"E19.4.3");var subQ21=sQuery(id+"F0.wireOp",EDGE,"E19.4.2");var subQ22=sQuery(id+"F0.wireOp",EDGE,"E19.4.1");var subQ23=sQuery(id+"F0.wireOp",EDGE,"E19.4.0");var subQ24=sQuery(id+"F0.wireOp",EDGE,"E19.3.5");var subQ25=sQuery(id+"F0.wireOp",EDGE,"E19.3.4");var subQ26=sQuery(id+"F0.wireOp",EDGE,"E19.3.3");var subQ27=sQuery(id+"F0.wireOp",EDGE,"E19.3.2");var subQ28=sQuery(id+"F0.wireOp",EDGE,"E19.3.1");var subQ29=sQuery(id+"F0.wireOp",EDGE,"E19.3.0");var subQ30=sQuery(id+"F0.wireOp",EDGE,"E19.2.5");var subQ31=sQuery(id+"F0.wireOp",EDGE,"E19.2.4");var subQ32=sQuery(id+"F0.wireOp",EDGE,"E19.2.3");var subQ33=sQuery(id+"F0.wireOp",EDGE,"E19.2.2");var subQ34=sQuery(id+"F0.wireOp",EDGE,"E19.2.1");var subQ35=sQuery(id+"F0.wireOp",EDGE,"E19.2.0");var subQ36=sQuery(id+"F0.wireOp",EDGE,"E19.1.5");var subQ37=sQuery(id+"F0.wireOp",EDGE,"E19.1.4");var subQ38=sQuery(id+"F0.wireOp",EDGE,"E19.1.3");var subQ39=sQuery(id+"F0.wireOp",EDGE,"E19.1.2");var subQ40=sQuery(id+"F0.wireOp",EDGE,"E19.1.1");var subQ41=sQuery(id+"F0.wireOp",EDGE,"E19.1.0");var subQ42=sQuery(id+"F0.wireOp",EDGE,"E18.filletArc");var subQ43=sQuery(id+"F0.wireOp",EDGE,"E17.filletArc");var subQ44=sQuery(id+"F0.wireOp",EDGE,"E16.trimOffspring");var subQ45=sQuery(id+"F0.wireOp",EDGE,"E15.trimOffspring");var subQ46=sQuery(id+"F0.wireOp",EDGE,"E14");var subQ47=sQuery(id+"F0.wireOp",EDGE,"E12.59.0");var subQ48=sQuery(id+"F0.wireOp",EDGE,"E12.58.0");var subQ49=sQuery(id+"F0.wireOp",EDGE,"E12.57.0");var subQ50=sQuery(id+"F0.wireOp",EDGE,"E12.56.0");var subQ51=sQuery(id+"F0.wireOp",EDGE,"E12.55.0");var subQ52=sQuery(id+"F0.wireOp",EDGE,"E12.54.0");var subQ53=sQuery(id+"F0.wireOp",EDGE,"E12.53.0");var subQ54=sQuery(id+"F0.wireOp",EDGE,"E12.52.0");var subQ55=sQuery(id+"F0.wireOp",EDGE,"E12.51.0");var subQ56=sQuery(id+"F0.wireOp",EDGE,"E12.50.0");var subQ57=sQuery(id+"F0.wireOp",EDGE,"E12.49.0");var subQ58=sQuery(id+"F0.wireOp",EDGE,"E12.48.0");var subQ59=sQuery(id+"F0.wireOp",EDGE,"E12.47.0");var subQ60=sQuery(id+"F0.wireOp",EDGE,"E12.46.0");var subQ61=sQuery(id+"F0.wireOp",EDGE,"E12.45.0");var subQ62=sQuery(id+"F0.wireOp",EDGE,"E12.44.0");var subQ63=sQuery(id+"F0.wireOp",EDGE,"E12.43.0");var subQ64=sQuery(id+"F0.wireOp",EDGE,"E12.42.0");var subQ65=sQuery(id+"F0.wireOp",EDGE,"E12.41.0");var subQ66=sQuery(id+"F0.wireOp",EDGE,"E12.40.0");var subQ67=sQuery(id+"F0.wireOp",EDGE,"E12.39.0");var subQ68=sQuery(id+"F0.wireOp",EDGE,"E12.38.0");var subQ69=sQuery(id+"F0.wireOp",EDGE,"E12.37.0");var subQ70=sQuery(id+"F0.wireOp",EDGE,"E12.36.0");var subQ71=sQuery(id+"F0.wireOp",EDGE,"E12.35.0");var subQ72=sQuery(id+"F0.wireOp",EDGE,"E12.34.0");var subQ73=sQuery(id+"F0.wireOp",EDGE,"E12.33.0");var subQ74=sQuery(id+"F0.wireOp",EDGE,"E12.32.0");var subQ75=sQuery(id+"F0.wireOp",EDGE,"E12.31.0");var subQ76=sQuery(id+"F0.wireOp",EDGE,"E12.30.0");var subQ77=sQuery(id+"F0.wireOp",EDGE,"E12.29.0");var subQ78=sQuery(id+"F0.wireOp",EDGE,"E12.28.0");var subQ79=sQuery(id+"F0.wireOp",EDGE,"E12.27.0");var subQ80=sQuery(id+"F0.wireOp",EDGE,"E12.26.0");var subQ81=sQuery(id+"F0.wireOp",EDGE,"E12.25.0");var subQ82=sQuery(id+"F0.wireOp",EDGE,"E12.24.0");var subQ83=sQuery(id+"F0.wireOp",EDGE,"E12.23.0");var subQ84=sQuery(id+"F0.wireOp",EDGE,"E12.22.0");var subQ85=sQuery(id+"F0.wireOp",EDGE,"E12.21.0");var subQ86=sQuery(id+"F0.wireOp",EDGE,"E12.20.0");var subQ87=sQuery(id+"F0.wireOp",EDGE,"E12.19.0");var subQ88=sQuery(id+"F0.wireOp",EDGE,"E12.18.0");var subQ89=sQuery(id+"F0.wireOp",EDGE,"E12.17.0");var subQ90=sQuery(id+"F0.wireOp",EDGE,"E12.16.0");var subQ91=sQuery(id+"F0.wireOp",EDGE,"E12.15.0");var subQ92=sQuery(id+"F0.wireOp",EDGE,"E12.14.0");var subQ93=sQuery(id+"F0.wireOp",EDGE,"E12.13.0");var subQ94=sQuery(id+"F0.wireOp",EDGE,"E12.12.0");var subQ95=sQuery(id+"F0.wireOp",EDGE,"E12.11.0");var subQ96=sQuery(id+"F0.wireOp",EDGE,"E12.10.0");var subQ97=sQuery(id+"F0.wireOp",EDGE,"E12.9.0");var subQ98=sQuery(id+"F0.wireOp",EDGE,"E12.8.0");var subQ99=sQuery(id+"F0.wireOp",EDGE,"E12.7.0");var subQ100=sQuery(id+"F0.wireOp",EDGE,"E12.6.0");var subQ101=sQuery(id+"F0.wireOp",EDGE,"E12.5.0");var subQ102=sQuery(id+"F0.wireOp",EDGE,"E12.4.0");var subQ103=sQuery(id+"F0.wireOp",EDGE,"E12.3.0");var subQ104=sQuery(id+"F0.wireOp",EDGE,"E12.2.0");var subQ105=sQuery(id+"F0.wireOp",EDGE,"E12.1.0");var subQ106=sQuery(id+"F0.wireOp",EDGE,"E11");var subQ107=sQuery(id+"F0.wireOp",EDGE,"E8");var subQ108=sQuery(id+"F0.wireOp",EDGE,"E7.59.5");var subQ109=sQuery(id+"F0.wireOp",EDGE,"E7.59.4");var subQ110=sQuery(id+"F0.wireOp",EDGE,"E7.59.3");var subQ111=sQuery(id+"F0.wireOp",EDGE,"E7.59.2");var subQ112=sQuery(id+"F0.wireOp",EDGE,"E7.59.1");var subQ113=sQuery(id+"F0.wireOp",EDGE,"E7.59.0");var subQ114=sQuery(id+"F0.wireOp",EDGE,"E7.58.5");var subQ115=sQuery(id+"F0.wireOp",EDGE,"E7.58.4");var subQ116=sQuery(id+"F0.wireOp",EDGE,"E7.58.3");var subQ117=sQuery(id+"F0.wireOp",EDGE,"E7.58.2");var subQ118=sQuery(id+"F0.wireOp",EDGE,"E7.58.1");var subQ119=sQuery(id+"F0.wireOp",EDGE,"E7.58.0");var subQ120=sQuery(id+"F0.wireOp",EDGE,"E7.57.5");var subQ121=sQuery(id+"F0.wireOp",EDGE,"E7.57.4");var subQ122=sQuery(id+"F0.wireOp",EDGE,"E7.57.3");var subQ123=sQuery(id+"F0.wireOp",EDGE,"E7.57.2");var subQ124=sQuery(id+"F0.wireOp",EDGE,"E7.57.1");var subQ125=sQuery(id+"F0.wireOp",EDGE,"E7.57.0");var subQ126=sQuery(id+"F0.wireOp",EDGE,"E7.56.5");var subQ127=sQuery(id+"F0.wireOp",EDGE,"E7.56.4");var subQ128=sQuery(id+"F0.wireOp",EDGE,"E7.56.3");var subQ129=sQuery(id+"F0.wireOp",EDGE,"E7.56.2");var subQ130=sQuery(id+"F0.wireOp",EDGE,"E7.56.1");var subQ131=sQuery(id+"F0.wireOp",EDGE,"E7.56.0");var subQ132=sQuery(id+"F0.wireOp",EDGE,"E7.55.5");var subQ133=sQuery(id+"F0.wireOp",EDGE,"E7.55.4");var subQ134=sQuery(id+"F0.wireOp",EDGE,"E7.55.3");var subQ135=sQuery(id+"F0.wireOp",EDGE,"E7.55.2");var subQ136=sQuery(id+"F0.wireOp",EDGE,"E7.55.1");var subQ137=sQuery(id+"F0.wireOp",EDGE,"E7.55.0");var subQ138=sQuery(id+"F0.wireOp",EDGE,"E7.54.5");var subQ139=sQuery(id+"F0.wireOp",EDGE,"E7.54.4");var subQ140=sQuery(id+"F0.wireOp",EDGE,"E7.54.3");var subQ141=sQuery(id+"F0.wireOp",EDGE,"E7.54.2");var subQ142=sQuery(id+"F0.wireOp",EDGE,"E7.54.1");var subQ143=sQuery(id+"F0.wireOp",EDGE,"E7.54.0");var subQ144=sQuery(id+"F0.wireOp",EDGE,"E7.53.5");var subQ145=sQuery(id+"F0.wireOp",EDGE,"E7.53.4");var subQ146=sQuery(id+"F0.wireOp",EDGE,"E7.53.3");var subQ147=sQuery(id+"F0.wireOp",EDGE,"E7.53.2");var subQ148=sQuery(id+"F0.wireOp",EDGE,"E7.53.1");var subQ149=sQuery(id+"F0.wireOp",EDGE,"E7.53.0");var subQ150=sQuery(id+"F0.wireOp",EDGE,"E7.52.5");var subQ151=sQuery(id+"F0.wireOp",EDGE,"E7.52.4");var subQ152=sQuery(id+"F0.wireOp",EDGE,"E7.52.3");var subQ153=sQuery(id+"F0.wireOp",EDGE,"E7.52.2");var subQ154=sQuery(id+"F0.wireOp",EDGE,"E7.52.1");var subQ155=sQuery(id+"F0.wireOp",EDGE,"E7.52.0");var subQ156=sQuery(id+"F0.wireOp",EDGE,"E7.51.5");var subQ157=sQuery(id+"F0.wireOp",EDGE,"E7.51.4");var subQ158=sQuery(id+"F0.wireOp",EDGE,"E7.51.3");var subQ159=sQuery(id+"F0.wireOp",EDGE,"E7.51.2");var subQ160=sQuery(id+"F0.wireOp",EDGE,"E7.51.1");var subQ161=sQuery(id+"F0.wireOp",EDGE,"E7.51.0");var subQ162=sQuery(id+"F0.wireOp",EDGE,"E7.50.5");var subQ163=sQuery(id+"F0.wireOp",EDGE,"E7.50.4");var subQ164=sQuery(id+"F0.wireOp",EDGE,"E7.50.3");var subQ165=sQuery(id+"F0.wireOp",EDGE,"E7.50.2");var subQ166=sQuery(id+"F0.wireOp",EDGE,"E7.50.1");var subQ167=sQuery(id+"F0.wireOp",EDGE,"E7.50.0");var subQ168=sQuery(id+"F0.wireOp",EDGE,"E7.49.5");var subQ169=sQuery(id+"F0.wireOp",EDGE,"E7.49.4");var subQ170=sQuery(id+"F0.wireOp",EDGE,"E7.49.3");var subQ171=sQuery(id+"F0.wireOp",EDGE,"E7.49.2");var subQ172=sQuery(id+"F0.wireOp",EDGE,"E7.49.1");var subQ173=sQuery(id+"F0.wireOp",EDGE,"E7.49.0");var subQ174=sQuery(id+"F0.wireOp",EDGE,"E7.48.5");var subQ175=sQuery(id+"F0.wireOp",EDGE,"E7.48.4");var subQ176=sQuery(id+"F0.wireOp",EDGE,"E7.48.3");var subQ177=sQuery(id+"F0.wireOp",EDGE,"E7.48.2");var subQ178=sQuery(id+"F0.wireOp",EDGE,"E7.48.1");var subQ179=sQuery(id+"F0.wireOp",EDGE,"E7.48.0");var subQ180=sQuery(id+"F0.wireOp",EDGE,"E7.47.5");var subQ181=sQuery(id+"F0.wireOp",EDGE,"E7.47.4");var subQ182=sQuery(id+"F0.wireOp",EDGE,"E7.47.3");var subQ183=sQuery(id+"F0.wireOp",EDGE,"E7.47.2");var subQ184=sQuery(id+"F0.wireOp",EDGE,"E7.47.1");var subQ185=sQuery(id+"F0.wireOp",EDGE,"E7.47.0");var subQ186=sQuery(id+"F0.wireOp",EDGE,"E7.46.5");var subQ187=sQuery(id+"F0.wireOp",EDGE,"E7.46.4");var subQ188=sQuery(id+"F0.wireOp",EDGE,"E7.46.3");var subQ189=sQuery(id+"F0.wireOp",EDGE,"E7.46.2");var subQ190=sQuery(id+"F0.wireOp",EDGE,"E7.46.1");var subQ191=sQuery(id+"F0.wireOp",EDGE,"E7.46.0");var subQ192=sQuery(id+"F0.wireOp",EDGE,"E7.45.5");var subQ193=sQuery(id+"F0.wireOp",EDGE,"E7.45.4");var subQ194=sQuery(id+"F0.wireOp",EDGE,"E7.45.3");var subQ195=sQuery(id+"F0.wireOp",EDGE,"E7.45.2");var subQ196=sQuery(id+"F0.wireOp",EDGE,"E7.45.1");var subQ197=sQuery(id+"F0.wireOp",EDGE,"E7.45.0");var subQ198=sQuery(id+"F0.wireOp",EDGE,"E7.44.5");var subQ199=sQuery(id+"F0.wireOp",EDGE,"E7.44.4");var subQ200=sQuery(id+"F0.wireOp",EDGE,"E7.44.3");var subQ201=sQuery(id+"F0.wireOp",EDGE,"E7.44.2");var subQ202=sQuery(id+"F0.wireOp",EDGE,"E7.44.1");var subQ203=sQuery(id+"F0.wireOp",EDGE,"E7.44.0");var subQ204=sQuery(id+"F0.wireOp",EDGE,"E7.43.5");var subQ205=sQuery(id+"F0.wireOp",EDGE,"E7.43.4");var subQ206=sQuery(id+"F0.wireOp",EDGE,"E7.43.3");var subQ207=sQuery(id+"F0.wireOp",EDGE,"E7.43.2");var subQ208=sQuery(id+"F0.wireOp",EDGE,"E7.43.1");var subQ209=sQuery(id+"F0.wireOp",EDGE,"E7.43.0");var subQ210=sQuery(id+"F0.wireOp",EDGE,"E7.42.5");var subQ211=sQuery(id+"F0.wireOp",EDGE,"E7.42.4");var subQ212=sQuery(id+"F0.wireOp",EDGE,"E7.42.3");var subQ213=sQuery(id+"F0.wireOp",EDGE,"E7.42.2");var subQ214=sQuery(id+"F0.wireOp",EDGE,"E7.42.1");var subQ215=sQuery(id+"F0.wireOp",EDGE,"E7.42.0");var subQ216=sQuery(id+"F0.wireOp",EDGE,"E7.41.5");var subQ217=sQuery(id+"F0.wireOp",EDGE,"E7.41.4");var subQ218=sQuery(id+"F0.wireOp",EDGE,"E7.41.3");var subQ219=sQuery(id+"F0.wireOp",EDGE,"E7.41.2");var subQ220=sQuery(id+"F0.wireOp",EDGE,"E7.41.1");var subQ221=sQuery(id+"F0.wireOp",EDGE,"E7.41.0");var subQ222=sQuery(id+"F0.wireOp",EDGE,"E7.40.5");var subQ223=sQuery(id+"F0.wireOp",EDGE,"E7.40.4");var subQ224=sQuery(id+"F0.wireOp",EDGE,"E7.40.3");var subQ225=sQuery(id+"F0.wireOp",EDGE,"E7.40.2");var subQ226=sQuery(id+"F0.wireOp",EDGE,"E7.40.1");var subQ227=sQuery(id+"F0.wireOp",EDGE,"E7.40.0");var subQ228=sQuery(id+"F0.wireOp",EDGE,"E7.39.5");var subQ229=sQuery(id+"F0.wireOp",EDGE,"E7.39.4");var subQ230=sQuery(id+"F0.wireOp",EDGE,"E7.39.3");var subQ231=sQuery(id+"F0.wireOp",EDGE,"E7.39.2");var subQ232=sQuery(id+"F0.wireOp",EDGE,"E7.39.1");var subQ233=sQuery(id+"F0.wireOp",EDGE,"E7.39.0");var subQ234=sQuery(id+"F0.wireOp",EDGE,"E7.38.5");var subQ235=sQuery(id+"F0.wireOp",EDGE,"E7.38.4");var subQ236=sQuery(id+"F0.wireOp",EDGE,"E7.38.3");var subQ237=sQuery(id+"F0.wireOp",EDGE,"E7.38.2");var subQ238=sQuery(id+"F0.wireOp",EDGE,"E7.38.1");var subQ239=sQuery(id+"F0.wireOp",EDGE,"E7.38.0");var subQ240=sQuery(id+"F0.wireOp",EDGE,"E7.37.5");var subQ241=sQuery(id+"F0.wireOp",EDGE,"E7.37.4");var subQ242=sQuery(id+"F0.wireOp",EDGE,"E7.37.3");var subQ243=sQuery(id+"F0.wireOp",EDGE,"E7.37.2");var subQ244=sQuery(id+"F0.wireOp",EDGE,"E7.37.1");var subQ245=sQuery(id+"F0.wireOp",EDGE,"E7.37.0");var subQ246=sQuery(id+"F0.wireOp",EDGE,"E7.36.5");var subQ247=sQuery(id+"F0.wireOp",EDGE,"E7.36.4");var subQ248=sQuery(id+"F0.wireOp",EDGE,"E7.36.3");var subQ249=sQuery(id+"F0.wireOp",EDGE,"E7.36.2");var subQ250=sQuery(id+"F0.wireOp",EDGE,"E7.36.1");var subQ251=sQuery(id+"F0.wireOp",EDGE,"E7.36.0");var subQ252=sQuery(id+"F0.wireOp",EDGE,"E7.35.5");var subQ253=sQuery(id+"F0.wireOp",EDGE,"E7.35.4");var subQ254=sQuery(id+"F0.wireOp",EDGE,"E7.35.3");var subQ255=sQuery(id+"F0.wireOp",EDGE,"E7.35.2");var subQ256=sQuery(id+"F0.wireOp",EDGE,"E7.35.1");var subQ257=sQuery(id+"F0.wireOp",EDGE,"E7.35.0");var subQ258=sQuery(id+"F0.wireOp",EDGE,"E7.34.5");var subQ259=sQuery(id+"F0.wireOp",EDGE,"E7.34.4");var subQ260=sQuery(id+"F0.wireOp",EDGE,"E7.34.3");var subQ261=sQuery(id+"F0.wireOp",EDGE,"E7.34.2");var subQ262=sQuery(id+"F0.wireOp",EDGE,"E7.34.1");var subQ263=sQuery(id+"F0.wireOp",EDGE,"E7.34.0");var subQ264=sQuery(id+"F0.wireOp",EDGE,"E7.33.5");var subQ265=sQuery(id+"F0.wireOp",EDGE,"E7.33.4");var subQ266=sQuery(id+"F0.wireOp",EDGE,"E7.33.3");var subQ267=sQuery(id+"F0.wireOp",EDGE,"E7.33.2");var subQ268=sQuery(id+"F0.wireOp",EDGE,"E7.33.1");var subQ269=sQuery(id+"F0.wireOp",EDGE,"E7.33.0");var subQ270=sQuery(id+"F0.wireOp",EDGE,"E7.32.5");var subQ271=sQuery(id+"F0.wireOp",EDGE,"E7.32.4");var subQ272=sQuery(id+"F0.wireOp",EDGE,"E7.32.3");var subQ273=sQuery(id+"F0.wireOp",EDGE,"E7.32.2");var subQ274=sQuery(id+"F0.wireOp",EDGE,"E7.32.1");var subQ275=sQuery(id+"F0.wireOp",EDGE,"E7.32.0");var subQ276=sQuery(id+"F0.wireOp",EDGE,"E7.31.5");var subQ277=sQuery(id+"F0.wireOp",EDGE,"E7.31.4");var subQ278=sQuery(id+"F0.wireOp",EDGE,"E7.31.3");var subQ279=sQuery(id+"F0.wireOp",EDGE,"E7.31.2");var subQ280=sQuery(id+"F0.wireOp",EDGE,"E7.31.1");var subQ281=sQuery(id+"F0.wireOp",EDGE,"E7.31.0");var subQ282=sQuery(id+"F0.wireOp",EDGE,"E7.30.5");var subQ283=sQuery(id+"F0.wireOp",EDGE,"E7.30.4");var subQ284=sQuery(id+"F0.wireOp",EDGE,"E7.30.3");var subQ285=sQuery(id+"F0.wireOp",EDGE,"E7.30.2");var subQ286=sQuery(id+"F0.wireOp",EDGE,"E7.30.1");var subQ287=sQuery(id+"F0.wireOp",EDGE,"E7.30.0");var subQ288=sQuery(id+"F0.wireOp",EDGE,"E7.29.5");var subQ289=sQuery(id+"F0.wireOp",EDGE,"E7.29.4");var subQ290=sQuery(id+"F0.wireOp",EDGE,"E7.29.3");var subQ291=sQuery(id+"F0.wireOp",EDGE,"E7.29.2");var subQ292=sQuery(id+"F0.wireOp",EDGE,"E7.29.1");var subQ293=sQuery(id+"F0.wireOp",EDGE,"E7.29.0");var subQ294=sQuery(id+"F0.wireOp",EDGE,"E7.28.5");var subQ295=sQuery(id+"F0.wireOp",EDGE,"E7.28.4");var subQ296=sQuery(id+"F0.wireOp",EDGE,"E7.28.3");var subQ297=sQuery(id+"F0.wireOp",EDGE,"E7.28.2");var subQ298=sQuery(id+"F0.wireOp",EDGE,"E7.28.1");var subQ299=sQuery(id+"F0.wireOp",EDGE,"E7.28.0");var subQ300=sQuery(id+"F0.wireOp",EDGE,"E7.27.5");var subQ301=sQuery(id+"F0.wireOp",EDGE,"E7.27.4");var subQ302=sQuery(id+"F0.wireOp",EDGE,"E7.27.3");var subQ303=sQuery(id+"F0.wireOp",EDGE,"E7.27.2");var subQ304=sQuery(id+"F0.wireOp",EDGE,"E7.27.1");var subQ305=sQuery(id+"F0.wireOp",EDGE,"E7.27.0");var subQ306=sQuery(id+"F0.wireOp",EDGE,"E7.26.5");var subQ307=sQuery(id+"F0.wireOp",EDGE,"E7.26.4");var subQ308=sQuery(id+"F0.wireOp",EDGE,"E7.26.3");var subQ309=sQuery(id+"F0.wireOp",EDGE,"E7.26.2");var subQ310=sQuery(id+"F0.wireOp",EDGE,"E7.26.1");var subQ311=sQuery(id+"F0.wireOp",EDGE,"E7.26.0");var subQ312=sQuery(id+"F0.wireOp",EDGE,"E7.25.5");var subQ313=sQuery(id+"F0.wireOp",EDGE,"E7.25.4");var subQ314=sQuery(id+"F0.wireOp",EDGE,"E7.25.3");var subQ315=sQuery(id+"F0.wireOp",EDGE,"E7.25.2");var subQ316=sQuery(id+"F0.wireOp",EDGE,"E7.25.1");var subQ317=sQuery(id+"F0.wireOp",EDGE,"E7.25.0");var subQ318=sQuery(id+"F0.wireOp",EDGE,"E7.24.5");var subQ319=sQuery(id+"F0.wireOp",EDGE,"E7.24.4");var subQ320=sQuery(id+"F0.wireOp",EDGE,"E7.24.3");var subQ321=sQuery(id+"F0.wireOp",EDGE,"E7.24.2");var subQ322=sQuery(id+"F0.wireOp",EDGE,"E7.24.1");var subQ323=sQuery(id+"F0.wireOp",EDGE,"E7.24.0");var subQ324=sQuery(id+"F0.wireOp",EDGE,"E7.23.5");var subQ325=sQuery(id+"F0.wireOp",EDGE,"E7.23.4");var subQ326=sQuery(id+"F0.wireOp",EDGE,"E7.23.3");var subQ327=sQuery(id+"F0.wireOp",EDGE,"E7.23.2");var subQ328=sQuery(id+"F0.wireOp",EDGE,"E7.23.1");var subQ329=sQuery(id+"F0.wireOp",EDGE,"E7.23.0");var subQ330=sQuery(id+"F0.wireOp",EDGE,"E7.22.5");var subQ331=sQuery(id+"F0.wireOp",EDGE,"E7.22.4");var subQ332=sQuery(id+"F0.wireOp",EDGE,"E7.22.3");var subQ333=sQuery(id+"F0.wireOp",EDGE,"E7.22.2");var subQ334=sQuery(id+"F0.wireOp",EDGE,"E7.22.1");var subQ335=sQuery(id+"F0.wireOp",EDGE,"E7.22.0");var subQ336=sQuery(id+"F0.wireOp",EDGE,"E7.21.5");var subQ337=sQuery(id+"F0.wireOp",EDGE,"E7.21.4");var subQ338=sQuery(id+"F0.wireOp",EDGE,"E7.21.3");var subQ339=sQuery(id+"F0.wireOp",EDGE,"E7.21.2");var subQ340=sQuery(id+"F0.wireOp",EDGE,"E7.21.1");var subQ341=sQuery(id+"F0.wireOp",EDGE,"E7.21.0");var subQ342=sQuery(id+"F0.wireOp",EDGE,"E7.20.5");var subQ343=sQuery(id+"F0.wireOp",EDGE,"E7.20.4");var subQ344=sQuery(id+"F0.wireOp",EDGE,"E7.20.3");var subQ345=sQuery(id+"F0.wireOp",EDGE,"E7.20.2");var subQ346=sQuery(id+"F0.wireOp",EDGE,"E7.20.1");var subQ347=sQuery(id+"F0.wireOp",EDGE,"E7.20.0");var subQ348=sQuery(id+"F0.wireOp",EDGE,"E7.19.5");var subQ349=sQuery(id+"F0.wireOp",EDGE,"E7.19.4");var subQ350=sQuery(id+"F0.wireOp",EDGE,"E7.19.3");var subQ351=sQuery(id+"F0.wireOp",EDGE,"E7.19.2");var subQ352=sQuery(id+"F0.wireOp",EDGE,"E7.19.1");var subQ353=sQuery(id+"F0.wireOp",EDGE,"E7.19.0");var subQ354=sQuery(id+"F0.wireOp",EDGE,"E7.18.5");var subQ355=sQuery(id+"F0.wireOp",EDGE,"E7.18.4");var subQ356=sQuery(id+"F0.wireOp",EDGE,"E7.18.3");var subQ357=sQuery(id+"F0.wireOp",EDGE,"E7.18.2");var subQ358=sQuery(id+"F0.wireOp",EDGE,"E7.18.1");var subQ359=sQuery(id+"F0.wireOp",EDGE,"E7.18.0");var subQ360=sQuery(id+"F0.wireOp",EDGE,"E7.17.5");var subQ361=sQuery(id+"F0.wireOp",EDGE,"E7.17.4");var subQ362=sQuery(id+"F0.wireOp",EDGE,"E7.17.3");var subQ363=sQuery(id+"F0.wireOp",EDGE,"E7.17.2");var subQ364=sQuery(id+"F0.wireOp",EDGE,"E7.17.1");var subQ365=sQuery(id+"F0.wireOp",EDGE,"E7.17.0");var subQ366=sQuery(id+"F0.wireOp",EDGE,"E7.16.5");var subQ367=sQuery(id+"F0.wireOp",EDGE,"E7.16.4");var subQ368=sQuery(id+"F0.wireOp",EDGE,"E7.16.3");var subQ369=sQuery(id+"F0.wireOp",EDGE,"E7.16.2");var subQ370=sQuery(id+"F0.wireOp",EDGE,"E7.16.1");var subQ371=sQuery(id+"F0.wireOp",EDGE,"E7.16.0");var subQ372=sQuery(id+"F0.wireOp",EDGE,"E7.15.5");var subQ373=sQuery(id+"F0.wireOp",EDGE,"E7.15.4");var subQ374=sQuery(id+"F0.wireOp",EDGE,"E7.15.3");var subQ375=sQuery(id+"F0.wireOp",EDGE,"E7.15.2");var subQ376=sQuery(id+"F0.wireOp",EDGE,"E7.15.1");var subQ377=sQuery(id+"F0.wireOp",EDGE,"E7.15.0");var subQ378=sQuery(id+"F0.wireOp",EDGE,"E7.14.5");var subQ379=sQuery(id+"F0.wireOp",EDGE,"E7.14.4");var subQ380=sQuery(id+"F0.wireOp",EDGE,"E7.14.3");var subQ381=sQuery(id+"F0.wireOp",EDGE,"E7.14.2");var subQ382=sQuery(id+"F0.wireOp",EDGE,"E7.14.1");var subQ383=sQuery(id+"F0.wireOp",EDGE,"E7.14.0");var subQ384=sQuery(id+"F0.wireOp",EDGE,"E7.13.5");var subQ385=sQuery(id+"F0.wireOp",EDGE,"E7.13.4");var subQ386=sQuery(id+"F0.wireOp",EDGE,"E7.13.3");var subQ387=sQuery(id+"F0.wireOp",EDGE,"E7.13.2");var subQ388=sQuery(id+"F0.wireOp",EDGE,"E7.13.1");var subQ389=sQuery(id+"F0.wireOp",EDGE,"E7.13.0");var subQ390=sQuery(id+"F0.wireOp",EDGE,"E7.12.5");var subQ391=sQuery(id+"F0.wireOp",EDGE,"E7.12.4");var subQ392=sQuery(id+"F0.wireOp",EDGE,"E7.12.3");var subQ393=sQuery(id+"F0.wireOp",EDGE,"E7.12.2");var subQ394=sQuery(id+"F0.wireOp",EDGE,"E7.12.1");var subQ395=sQuery(id+"F0.wireOp",EDGE,"E7.12.0");var subQ396=sQuery(id+"F0.wireOp",EDGE,"E7.11.5");var subQ397=sQuery(id+"F0.wireOp",EDGE,"E7.11.4");var subQ398=sQuery(id+"F0.wireOp",EDGE,"E7.11.3");var subQ399=sQuery(id+"F0.wireOp",EDGE,"E7.11.2");var subQ400=sQuery(id+"F0.wireOp",EDGE,"E7.11.1");var subQ401=sQuery(id+"F0.wireOp",EDGE,"E7.11.0");var subQ402=sQuery(id+"F0.wireOp",EDGE,"E7.10.5");var subQ403=sQuery(id+"F0.wireOp",EDGE,"E7.10.4");var subQ404=sQuery(id+"F0.wireOp",EDGE,"E7.10.3");var subQ405=sQuery(id+"F0.wireOp",EDGE,"E7.10.2");var subQ406=sQuery(id+"F0.wireOp",EDGE,"E7.10.1");var subQ407=sQuery(id+"F0.wireOp",EDGE,"E7.10.0");var subQ408=sQuery(id+"F0.wireOp",EDGE,"E7.9.5");var subQ409=sQuery(id+"F0.wireOp",EDGE,"E7.9.4");var subQ410=sQuery(id+"F0.wireOp",EDGE,"E7.9.3");var subQ411=sQuery(id+"F0.wireOp",EDGE,"E7.9.2");var subQ412=sQuery(id+"F0.wireOp",EDGE,"E7.9.1");var subQ413=sQuery(id+"F0.wireOp",EDGE,"E7.9.0");var subQ414=sQuery(id+"F0.wireOp",EDGE,"E7.8.5");var subQ415=sQuery(id+"F0.wireOp",EDGE,"E7.8.4");var subQ416=sQuery(id+"F0.wireOp",EDGE,"E7.8.3");var subQ417=sQuery(id+"F0.wireOp",EDGE,"E7.8.2");var subQ418=sQuery(id+"F0.wireOp",EDGE,"E7.8.1");var subQ419=sQuery(id+"F0.wireOp",EDGE,"E7.8.0");var subQ420=sQuery(id+"F0.wireOp",EDGE,"E7.7.5");var subQ421=sQuery(id+"F0.wireOp",EDGE,"E7.7.4");var subQ422=sQuery(id+"F0.wireOp",EDGE,"E7.7.3");var subQ423=sQuery(id+"F0.wireOp",EDGE,"E7.7.2");var subQ424=sQuery(id+"F0.wireOp",EDGE,"E7.7.1");var subQ425=sQuery(id+"F0.wireOp",EDGE,"E7.7.0");var subQ426=sQuery(id+"F0.wireOp",EDGE,"E7.6.5");var subQ427=sQuery(id+"F0.wireOp",EDGE,"E7.6.4");var subQ428=sQuery(id+"F0.wireOp",EDGE,"E7.6.3");var subQ429=sQuery(id+"F0.wireOp",EDGE,"E7.6.2");var subQ430=sQuery(id+"F0.wireOp",EDGE,"E7.6.1");var subQ431=sQuery(id+"F0.wireOp",EDGE,"E7.6.0");var subQ432=sQuery(id+"F0.wireOp",EDGE,"E7.5.5");var subQ433=sQuery(id+"F0.wireOp",EDGE,"E7.5.4");var subQ434=sQuery(id+"F0.wireOp",EDGE,"E7.5.3");var subQ435=sQuery(id+"F0.wireOp",EDGE,"E7.5.2");var subQ436=sQuery(id+"F0.wireOp",EDGE,"E7.5.1");var subQ437=sQuery(id+"F0.wireOp",EDGE,"E7.5.0");var subQ438=sQuery(id+"F0.wireOp",EDGE,"E7.4.5");var subQ439=sQuery(id+"F0.wireOp",EDGE,"E7.4.4");var subQ440=sQuery(id+"F0.wireOp",EDGE,"E7.4.3");var subQ441=sQuery(id+"F0.wireOp",EDGE,"E7.4.2");var subQ442=sQuery(id+"F0.wireOp",EDGE,"E7.4.1");var subQ443=sQuery(id+"F0.wireOp",EDGE,"E7.4.0");var subQ444=sQuery(id+"F0.wireOp",EDGE,"E7.3.5");var subQ445=sQuery(id+"F0.wireOp",EDGE,"E7.3.4");var subQ446=sQuery(id+"F0.wireOp",EDGE,"E7.3.3");var subQ447=sQuery(id+"F0.wireOp",EDGE,"E7.3.2");var subQ448=sQuery(id+"F0.wireOp",EDGE,"E7.3.1");var subQ449=sQuery(id+"F0.wireOp",EDGE,"E7.3.0");var subQ450=sQuery(id+"F0.wireOp",EDGE,"E7.2.5");var subQ451=sQuery(id+"F0.wireOp",EDGE,"E7.2.4");var subQ452=sQuery(id+"F0.wireOp",EDGE,"E7.2.3");var subQ453=sQuery(id+"F0.wireOp",EDGE,"E7.2.2");var subQ454=sQuery(id+"F0.wireOp",EDGE,"E7.2.1");var subQ455=sQuery(id+"F0.wireOp",EDGE,"E7.2.0");var subQ456=sQuery(id+"F0.wireOp",EDGE,"E7.1.5");var subQ457=sQuery(id+"F0.wireOp",EDGE,"E7.1.4");var subQ458=sQuery(id+"F0.wireOp",EDGE,"E7.1.3");var subQ459=sQuery(id+"F0.wireOp",EDGE,"E7.1.2");var subQ460=sQuery(id+"F0.wireOp",EDGE,"E7.1.1");var subQ461=sQuery(id+"F0.wireOp",EDGE,"E7.1.0");var subQ462=sQuery(id+"F0.wireOp",EDGE,"E6.MirrorCS");var subQ463=sQuery(id+"F0.wireOp",EDGE,"E5.MirrorCS");var subQ464=sQuery(id+"F0.wireOp",EDGE,"E4.MirrorCS");var subQ465=sQuery(id+"F0.wireOp",EDGE,"E3");var subQ466=sQuery(id+"F0.wireOp",EDGE,"E2");var subQ467=sQuery(id+"F0.wireOp",EDGE,"E1");var subQ468=sQuery(id+"F0.wireOp",EDGE,"E0");Q8=makeQuery(id+"F2.boolean.opBoolean","MERGE",FACE,{"derivedFrom":[makeQuery(id+"F1.opExtrude","CAP_FACE",FACE,{"disambiguationData":[OSD([subQ468,subQ467,subQ466,subQ465,subQ464,subQ463,subQ462,subQ461,subQ460,subQ459,subQ458,subQ457,subQ456,subQ455,subQ454,subQ453,subQ452,subQ451,subQ450,subQ449,subQ448,subQ447,subQ446,subQ445,subQ444,subQ443,subQ442,subQ441,subQ440,subQ439,subQ438,subQ437,subQ436,subQ435,subQ434,subQ433,subQ432,subQ431,subQ430,subQ429,subQ428,subQ427,subQ426,subQ425,subQ424,subQ423,subQ422,subQ421,subQ420,subQ419,subQ418,subQ417,subQ416,subQ415,subQ414,subQ413,subQ412,subQ411,subQ410,subQ409,subQ408,subQ407,subQ406,subQ405,subQ404,subQ403,subQ402,subQ401,subQ400,subQ399,subQ398,subQ397,subQ396,subQ395,subQ394,subQ393,subQ392,subQ391,subQ390,subQ389,subQ388,subQ387,subQ386,subQ385,subQ384,subQ383,subQ382,subQ381,subQ380,subQ379,subQ378,subQ377,subQ376,subQ375,subQ374,subQ373,subQ372,subQ371,subQ370,subQ369,subQ368,subQ367,subQ366,subQ365,subQ364,subQ363,subQ362,subQ361,subQ360,subQ359,subQ358,subQ357,subQ356,subQ355,subQ354,subQ353,subQ352,subQ351,subQ350,subQ349,subQ348,subQ347,subQ346,subQ345,subQ344,subQ343,subQ342,subQ341,subQ340,subQ339,subQ338,subQ337,subQ336,subQ335,subQ334,subQ333,subQ332,subQ331,subQ330,subQ329,subQ328,subQ327,subQ326,subQ325,subQ324,subQ323,subQ322,subQ321,subQ320,subQ319,subQ318,subQ317,subQ316,subQ315,subQ314,subQ313,subQ312,subQ311,subQ310,subQ309,subQ308,subQ307,subQ306,subQ305,subQ304,subQ303,subQ302,subQ301,subQ300,subQ299,subQ298,subQ297,subQ296,subQ295,subQ294,subQ293,subQ292,subQ291,subQ290,subQ289,subQ288,subQ287,subQ286,subQ285,subQ284,subQ283,subQ282,subQ281,subQ280,subQ279,subQ278,subQ277,subQ276,subQ275,subQ274,subQ273,subQ272,subQ271,subQ270,subQ269,subQ268,subQ267,subQ266,subQ265,subQ264,subQ263,subQ262,subQ261,subQ260,subQ259,subQ258,subQ257,subQ256,subQ255,subQ254,subQ253,subQ252,subQ251,subQ250,subQ249,subQ248,subQ247,subQ246,subQ245,subQ244,subQ243,subQ242,subQ241,subQ240,subQ239,subQ238,subQ237,subQ236,subQ235,subQ234,subQ233,subQ232,subQ231,subQ230,subQ229,subQ228,subQ227,subQ226,subQ225,subQ224,subQ223,subQ222,subQ221,subQ220,subQ219,subQ218,subQ217,subQ216,subQ215,subQ214,subQ213,subQ212,subQ211,subQ210,subQ209,subQ208,subQ207,subQ206,subQ205,subQ204,subQ203,subQ202,subQ201,subQ200,subQ199,subQ198,subQ197,subQ196,subQ195,subQ194,subQ193,subQ192,subQ191,subQ190,subQ189,subQ188,subQ187,subQ186,subQ185,subQ184,subQ183,subQ182,subQ181,subQ180,subQ179,subQ178,subQ177,subQ176,subQ175,subQ174,subQ173,subQ172,subQ171,subQ170,subQ169,subQ168,subQ167,subQ166,subQ165,subQ164,subQ163,subQ162,subQ161,subQ160,subQ159,subQ158,subQ157,subQ156,subQ155,subQ154,subQ153,subQ152,subQ151,subQ150,subQ149,subQ148,subQ147,subQ146,subQ145,subQ144,subQ143,subQ142,subQ141,subQ140,subQ139,subQ138,subQ137,subQ136,subQ135,subQ134,subQ133,subQ132,subQ131,subQ130,subQ129,subQ128,subQ127,subQ126,subQ125,subQ124,subQ123,subQ122,subQ121,subQ120,subQ119,subQ118,subQ117,subQ116,subQ115,subQ114,subQ113,subQ112,subQ111,subQ110,subQ109,subQ108,subQ107,subQ106,subQ105,subQ104,subQ103,subQ102,subQ101,subQ100,subQ99,subQ98,subQ97,subQ96,subQ95,subQ94,subQ93,subQ92,subQ91,subQ90,subQ89,subQ88,subQ87,subQ86,subQ85,subQ84,subQ83,subQ82,subQ81,subQ80,subQ79,subQ78,subQ77,subQ76,subQ75,subQ74,subQ73,subQ72,subQ71,subQ70,subQ69,subQ68,subQ67,subQ66,subQ65,subQ64,subQ63,subQ62,subQ61,subQ60,subQ59,subQ58,subQ57,subQ56,subQ55,subQ54,subQ53,subQ52,subQ51,subQ50,subQ49,subQ48,subQ47,subQ46,subQ45,subQ44,subQ43,subQ42,subQ41,subQ40,subQ39,subQ38,subQ37,subQ36,subQ35,subQ34,subQ33,subQ32,subQ31,subQ30,subQ29,subQ28,subQ27,subQ26,subQ25,subQ24,subQ23,subQ22,subQ21,subQ20,subQ19,subQ18,subQ17,subQ16,subQ15,subQ14,subQ13,subQ12,subQ11,subQ10,subQ9,subQ8,subQ7,subQ6,subQ5,subQ4,subQ3,subQ2,subQ1,subQ0])],"isStart":true}),makeQuery(id+"F2.opExtrude","CAP_FACE",FACE,{"disambiguationData":[OSD([subQ468,subQ467,subQ466,subQ465,subQ464,subQ463,subQ462,subQ461,subQ460,subQ459,subQ458,subQ457,subQ456,subQ455,subQ454,subQ453,subQ452,subQ451,subQ450,subQ449,subQ448,subQ447,subQ446,subQ445,subQ444,subQ443,subQ442,subQ441,subQ440,subQ439,subQ438,subQ437,subQ436,subQ435,subQ434,subQ433,subQ432,subQ431,subQ430,subQ429,subQ428,subQ427,subQ426,subQ425,subQ424,subQ423,subQ422,subQ421,subQ420,subQ419,subQ418,subQ417,subQ416,subQ415,subQ414,subQ413,subQ412,subQ411,subQ410,subQ409,subQ408,subQ407,subQ406,subQ405,subQ404,subQ403,subQ402,subQ401,subQ400,subQ399,subQ398,subQ397,subQ396,subQ395,subQ394,subQ393,subQ392,subQ391,subQ390,subQ389,subQ388,subQ387,subQ386,subQ385,subQ384,subQ383,subQ382,subQ381,subQ380,subQ379,subQ378,subQ377,subQ376,subQ375,subQ374,subQ373,subQ372,subQ371,subQ370,subQ369,subQ368,subQ367,subQ366,subQ365,subQ364,subQ363,subQ362,subQ361,subQ360,subQ359,subQ358,subQ357,subQ356,subQ355,subQ354,subQ353,subQ352,subQ351,subQ350,subQ349,subQ348,subQ347,subQ346,subQ345,subQ344,subQ343,subQ342,subQ341,subQ340,subQ339,subQ338,subQ337,subQ336,subQ335,subQ334,subQ333,subQ332,subQ331,subQ330,subQ329,subQ328,subQ327,subQ326,subQ325,subQ324,subQ323,subQ322,subQ321,subQ320,subQ319,subQ318,subQ317,subQ316,subQ315,subQ314,subQ313,subQ312,subQ311,subQ310,subQ309,subQ308,subQ307,subQ306,subQ305,subQ304,subQ303,subQ302,subQ301,subQ300,subQ299,subQ298,subQ297,subQ296,subQ295,subQ294,subQ293,subQ292,subQ291,subQ290,subQ289,subQ288,subQ287,subQ286,subQ285,subQ284,subQ283,subQ282,subQ281,subQ280,subQ279,subQ278,subQ277,subQ276,subQ275,subQ274,subQ273,subQ272,subQ271,subQ270,subQ269,subQ268,subQ267,subQ266,subQ265,subQ264,subQ263,subQ262,subQ261,subQ260,subQ259,subQ258,subQ257,subQ256,subQ255,subQ254,subQ253,subQ252,subQ251,subQ250,subQ249,subQ248,subQ247,subQ246,subQ245,subQ244,subQ243,subQ242,subQ241,subQ240,subQ239,subQ238,subQ237,subQ236,subQ235,subQ234,subQ233,subQ232,subQ231,subQ230,subQ229,subQ228,subQ227,subQ226,subQ225,subQ224,subQ223,subQ222,subQ221,subQ220,subQ219,subQ218,subQ217,subQ216,subQ215,subQ214,subQ213,subQ212,subQ211,subQ210,subQ209,subQ208,subQ207,subQ206,subQ205,subQ204,subQ203,subQ202,subQ201,subQ200,subQ199,subQ198,subQ197,subQ196,subQ195,subQ194,subQ193,subQ192,subQ191,subQ190,subQ189,subQ188,subQ187,subQ186,subQ185,subQ184,subQ183,subQ182,subQ181,subQ180,subQ179,subQ178,subQ177,subQ176,subQ175,subQ174,subQ173,subQ172,subQ171,subQ170,subQ169,subQ168,subQ167,subQ166,subQ165,subQ164,subQ163,subQ162,subQ161,subQ160,subQ159,subQ158,subQ157,subQ156,subQ155,subQ154,subQ153,subQ152,subQ151,subQ150,subQ149,subQ148,subQ147,subQ146,subQ145,subQ144,subQ143,subQ142,subQ141,subQ140,subQ139,subQ138,subQ137,subQ136,subQ135,subQ134,subQ133,subQ132,subQ131,subQ130,subQ129,subQ128,subQ127,subQ126,subQ125,subQ124,subQ123,subQ122,subQ121,subQ120,subQ119,subQ118,subQ117,subQ116,subQ115,subQ114,subQ113,subQ112,subQ111,subQ110,subQ109,subQ108,subQ107,subQ106,subQ105,subQ104,subQ103,subQ102,subQ101,subQ100,subQ99,subQ98,subQ97,subQ96,subQ95,subQ94,subQ93,subQ92,subQ91,subQ90,subQ89,subQ88,subQ87,subQ86,subQ85,subQ84,subQ83,subQ82,subQ81,subQ80,subQ79,subQ78,subQ77,subQ76,subQ75,subQ74,subQ73,subQ72,subQ71,subQ70,subQ69,subQ68,subQ67,subQ66,subQ65,subQ64,subQ63,subQ62,subQ61,subQ60,subQ59,subQ58,subQ57,subQ56,subQ55,subQ54,subQ53,subQ52,subQ51,subQ50,subQ49,subQ48,subQ47,subQ46,subQ45,subQ44,subQ43,subQ42,subQ41,subQ40,subQ39,subQ38,subQ37,subQ36,subQ35,subQ34,subQ33,subQ32,subQ31,subQ30,subQ29,subQ28,subQ27,subQ26,subQ25,subQ24,subQ23,subQ22,subQ21,subQ20,subQ19,subQ18,subQ17,subQ16,subQ15,subQ14,subQ13,subQ12,subQ11,subQ10,subQ9,subQ8,subQ7,subQ6,subQ5,subQ4,subQ3,subQ2,subQ1,subQ0])],"isStart":true})]});}
            fillet(context, id + "F3", {"entities" : qUnion([Q0, Q1, Q2, Q3, Q4, Q5, Q6, Q7, Q8]), "radius" : .5 * mm, "tangentPropagation" : true, "allowEdgeOverflow" : false});
        }
    });
